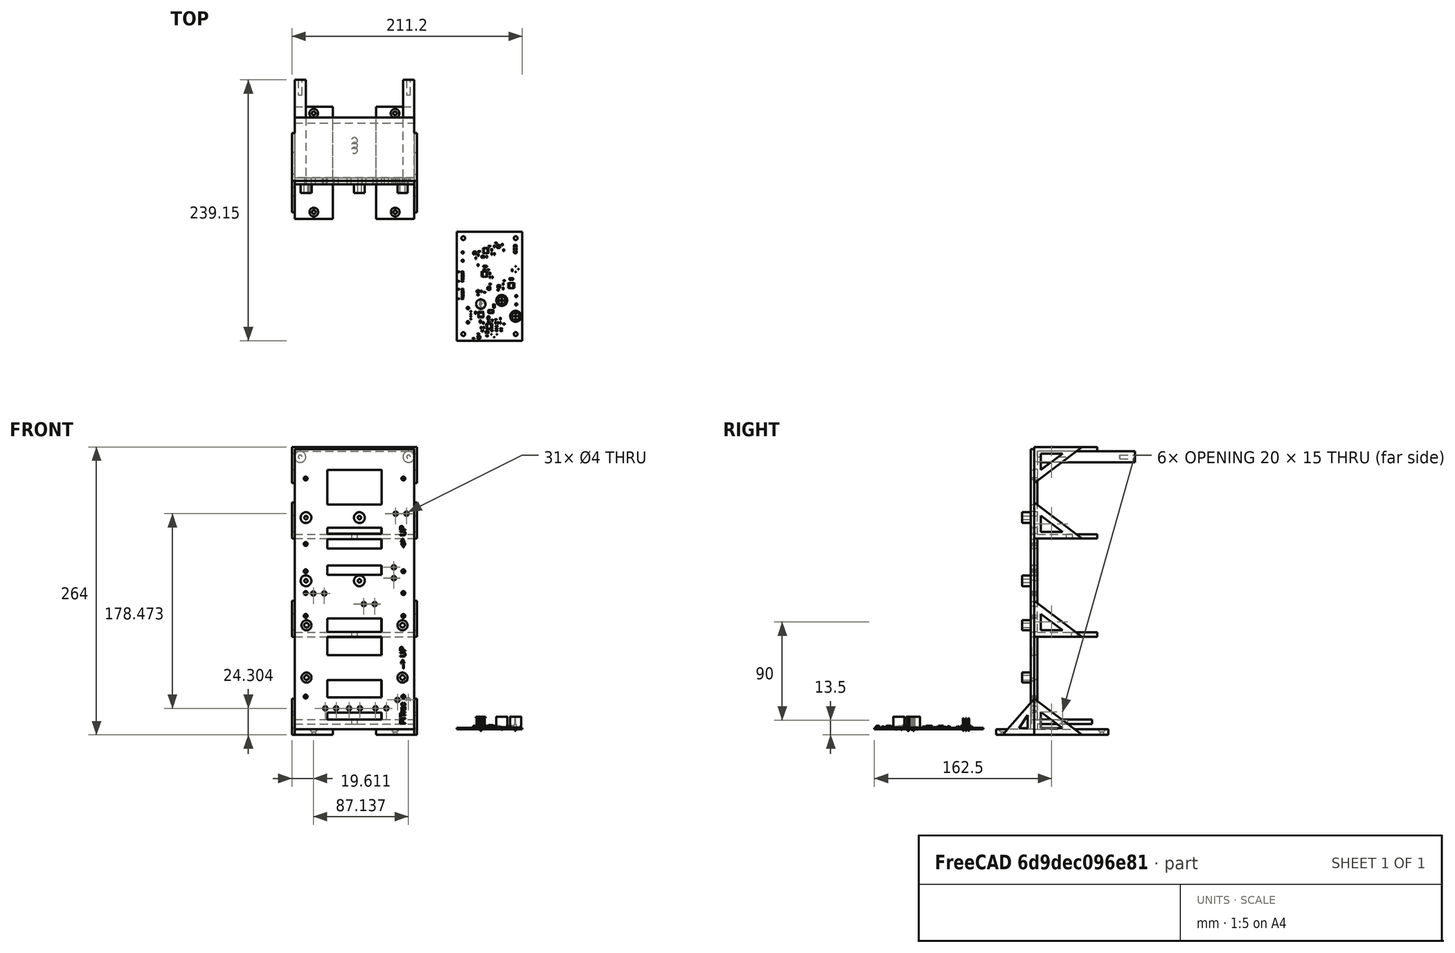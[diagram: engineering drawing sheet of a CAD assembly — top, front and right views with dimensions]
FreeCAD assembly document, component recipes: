
FREECAD ASSEMBLY — COMPONENT RECIPES ("Tower")

This assembly document has 2 components, labeled P0..P1 below (a component is one placed body or linked part). 1 of them carries a construction recipe — the FreeCAD feature program that regenerates the part from scratch, quoted from this document or its linked companion documents; the rest are supplied as boundary geometry only. No exploded tour is included for this assembly.
COMPONENT P0 — recipe-attached ("Tower Part -V2  Connector Board Variant", modeled in this document).
Construction recipe (the document's own serialized feature program — sketch geometry with constraints, then the solid features built on it; lengths are millimeters unless a unit is written):

FEATURE [Sketcher::SketchObject] Sketch  label="Backplate Sketch"
  ArcFitTolerance = 1e-06
  AttachmentSupport = -> [XZ_Plane001]
  FullyConstrained = false
  MakeInternals = false
  MapMode = 5
  Placement = pos=(0,0,0) rot=(1,0,0;1.5708rad)
  expr: Constraints[10] = <<Monitor Chassis Parameters>>.GSBackPlateBoltDiameter
  expr: Constraints[11] = <<Monitor Chassis Parameters>>.GSComputeBoardWidth / 2 - <<Monitor Chassis Parameters>>.GSBackPlateOuterHolesInsetFromSide
  expr: Constraints[129] = <<Monitor Chassis Parameters>>.GSTowerTieDownHoleSeparation
  expr: Constraints[15] = <<Monitor Chassis Parameters>>.GSBackPlateWidthIncrement
  expr: Constraints[55] = <<Monitor Chassis Parameters>>.GSBackPlateLengthIncrement
  expr: Constraints[59] = <<Monitor Chassis Parameters>>.GSBackPlateWidth
  expr: Constraints[71] = 1.5 * <<Monitor Chassis Parameters>>.GSBackPlateMinimumSpanWidth
  expr: Constraints[72] = 1.5 * <<Monitor Chassis Parameters>>.GSBackPlateMinimumSpanWidth
  expr: Constraints[7] = <<Monitor Chassis Parameters>>.GSComputeBoardHeight
  expr: Constraints[80] = <<Monitor Chassis Parameters>>.GSBackPlateLengthIncrement
  expr: Constraints[8] = <<Monitor Chassis Parameters>>.GSComputeBoardWidth
  expr: Constraints[97] = <<Monitor Chassis Parameters>>.GSTowerTieDownHoleDiameter
  expr: Constraints[98] = <<Monitor Chassis Parameters>>.GSTowerTieDownHoleDiameter
  expr: Constraints[99] = <<Monitor Chassis Parameters>>.GSTowerTieDownHoleSeparation
  expr: Constraints[9] = <<Monitor Chassis Parameters>>.GSComputeBoardWidth / 2
  sketch-geometry (63):
    g0: LineSegment [constr] StartX=-50.8 StartY=24.4067 StartZ=0 EndX=50.8 EndY=24.4067 EndZ=0
    g1: LineSegment [constr] StartX=50.8 StartY=24.4067 StartZ=0 EndX=50.8 EndY=253.007 EndZ=0
    g2: LineSegment [constr] StartX=50.8 StartY=253.007 StartZ=0 EndX=-50.8 EndY=253.007 EndZ=0
    g3: LineSegment [constr] StartX=-50.8 StartY=253.007 StartZ=0 EndX=-50.8 EndY=24.4067 EndZ=0
    g4: Circle CenterX=46.99 CenterY=45.5 CenterZ=0 NormalX=0 NormalY=0 NormalZ=1 AngleXU=0 Radius=1.4
    g5: LineSegment StartX=-54.8 StartY=257.007 StartZ=0 EndX=-54.8 EndY=20.4067 EndZ=0
    g6: LineSegment [constr] StartX=-54.8 StartY=20.4067 StartZ=0 EndX=54.8 EndY=20.4067 EndZ=0
    g7: LineSegment StartX=24.8 StartY=141.727 StartZ=0 EndX=-24.8 EndY=141.727 EndZ=0
    g8: LineSegment StartX=-24.8 StartY=141.727 StartZ=0 EndX=-24.8 EndY=150.228 EndZ=0
    g9: LineSegment StartX=-24.8 StartY=150.228 StartZ=0 EndX=24.8 EndY=150.228 EndZ=0
    g10: LineSegment StartX=24.8 StartY=150.228 StartZ=0 EndX=24.8 EndY=141.727 EndZ=0
    g11: LineSegment StartX=24.8 StartY=238.088 StartZ=0 EndX=-24.8 EndY=238.088 EndZ=0
    g12: LineSegment StartX=-24.8 StartY=238.088 StartZ=0 EndX=-24.8 EndY=206.336 EndZ=0
    g13: LineSegment StartX=-24.8 StartY=206.336 StartZ=0 EndX=24.8 EndY=206.336 EndZ=0
    g14: LineSegment StartX=24.8 StartY=206.336 StartZ=0 EndX=24.8 EndY=238.088 EndZ=0
    g15: LineSegment StartX=-24.8 StartY=184.895 StartZ=0 EndX=-24.8 EndY=179.263 EndZ=0
    g16: LineSegment StartX=-24.8 StartY=179.263 StartZ=0 EndX=24.8 EndY=179.263 EndZ=0
    g17: LineSegment StartX=24.8 StartY=179.263 StartZ=0 EndX=24.8 EndY=184.895 EndZ=0
    g18: LineSegment StartX=24.8 StartY=184.895 StartZ=0 EndX=-24.8 EndY=184.895 EndZ=0
    g19: LineSegment StartX=-24.8 StartY=84.8648 StartZ=0 EndX=-24.8 EndY=68.0887 EndZ=0
    g20: LineSegment StartX=-24.8 StartY=68.0887 StartZ=0 EndX=24.8 EndY=68.0887 EndZ=0
    g21: LineSegment StartX=24.8 StartY=68.0887 StartZ=0 EndX=24.8 EndY=84.8648 EndZ=0
    g22: LineSegment StartX=24.8 StartY=84.8648 StartZ=0 EndX=-24.8 EndY=84.8648 EndZ=0
    g23: LineSegment StartX=-24.8 StartY=45.1663 StartZ=0 EndX=-24.8 EndY=29.2968 EndZ=0
    g24: LineSegment StartX=24.8 StartY=29.2968 StartZ=0 EndX=24.8 EndY=45.1663 EndZ=0
    g25: LineSegment StartX=54.8 StartY=20.4067 StartZ=0 EndX=54.8 EndY=257.007 EndZ=0
    g26: LineSegment StartX=-54.8 StartY=257.007 StartZ=0 EndX=54.8 EndY=257.007 EndZ=0
    g27: LineSegment StartX=-54.8 StartY=20.4067 StartZ=0 EndX=-54.8 EndY=0 EndZ=0
    g28: LineSegment StartX=-54.8 StartY=0 StartZ=0 EndX=54.8 EndY=0 EndZ=0
    g29: LineSegment StartX=54.8 StartY=0 StartZ=0 EndX=54.8 EndY=20.4067 EndZ=0
    g30: LineSegment [constr] StartX=54.8 StartY=20.4067 StartZ=0 EndX=-54.8 EndY=20.4067 EndZ=0
    g31: LineSegment StartX=-24.8 StartY=45.1663 StartZ=0 EndX=24.8 EndY=45.1663 EndZ=0
    g32: LineSegment StartX=-24.8 StartY=29.2968 StartZ=0 EndX=24.8 EndY=29.2968 EndZ=0
    g33: LineSegment StartX=-24.8 StartY=15.5143 StartZ=0 EndX=-24.8 EndY=9.05652 EndZ=0
    g34: LineSegment StartX=-24.8 StartY=9.05652 StartZ=0 EndX=24.8 EndY=9.05652 EndZ=0
    g35: LineSegment StartX=24.8 StartY=9.05652 StartZ=0 EndX=24.8 EndY=15.5143 EndZ=0
    g36: LineSegment StartX=24.8 StartY=15.5143 StartZ=0 EndX=-24.8 EndY=15.5143 EndZ=0
    g37: Circle CenterX=37.7226 CenterY=197.777 CenterZ=0 NormalX=0 NormalY=0 NormalZ=1 AngleXU=0 Radius=2
    g38: Circle CenterX=47.7226 CenterY=197.777 CenterZ=0 NormalX=0 NormalY=0 NormalZ=1 AngleXU=0 Radius=2
    g39: Circle CenterX=-4.99066 CenterY=19.304 CenterZ=0 NormalX=0 NormalY=0 NormalZ=1 AngleXU=0 Radius=2
    g40: Circle CenterX=5.00934 CenterY=19.304 CenterZ=0 NormalX=0 NormalY=0 NormalZ=1 AngleXU=0 Radius=2
    g41: Circle CenterX=19.2048 CenterY=19.304 CenterZ=0 NormalX=0 NormalY=0 NormalZ=1 AngleXU=0 Radius=2
    g42: Circle CenterX=29.2048 CenterY=19.304 CenterZ=0 NormalX=0 NormalY=0 NormalZ=1 AngleXU=0 Radius=2
    g43: Circle CenterX=39.3678 CenterY=26.9682 CenterZ=0 NormalX=0 NormalY=0 NormalZ=1 AngleXU=0 Radius=2
    g44: Circle CenterX=49.3678 CenterY=26.9682 CenterZ=0 NormalX=0 NormalY=0 NormalZ=1 AngleXU=0 Radius=2
    g45: Circle CenterX=-37.7708 CenterY=124.614 CenterZ=0 NormalX=0 NormalY=0 NormalZ=1 AngleXU=0 Radius=2
    g46: Circle CenterX=-27.7708 CenterY=124.614 CenterZ=0 NormalX=0 NormalY=0 NormalZ=1 AngleXU=0 Radius=2
    g47: Circle CenterX=-26.8243 CenterY=19.304 CenterZ=0 NormalX=0 NormalY=0 NormalZ=1 AngleXU=0 Radius=2
    g48: Circle CenterX=-16.8243 CenterY=19.304 CenterZ=0 NormalX=0 NormalY=0 NormalZ=1 AngleXU=0 Radius=2
    g49: Circle CenterX=36.1106 CenterY=138.665 CenterZ=0 NormalX=0 NormalY=0 NormalZ=1 AngleXU=0 Radius=2
    g50: Circle CenterX=36.1106 CenterY=148.665 CenterZ=0 NormalX=0 NormalY=0 NormalZ=1 AngleXU=0 Radius=2
    g51: Circle CenterX=49.3678 CenterY=26.9682 CenterZ=0 NormalX=0 NormalY=0 NormalZ=1 AngleXU=0 Radius=2
    g52: Circle CenterX=8.52821 CenterY=114.871 CenterZ=0 NormalX=0 NormalY=0 NormalZ=1 AngleXU=0 Radius=2
    g53: Circle CenterX=18.5282 CenterY=114.871 CenterZ=0 NormalX=0 NormalY=0 NormalZ=1 AngleXU=0 Radius=2
    g54: Circle CenterX=49.3678 CenterY=26.9682 CenterZ=0 NormalX=0 NormalY=0 NormalZ=1 AngleXU=0 Radius=2
    g55: LineSegment StartX=-24.8 StartY=174.457 StartZ=0 EndX=-24.8 EndY=165.919 EndZ=0
    g56: LineSegment StartX=-24.8 StartY=165.919 StartZ=0 EndX=24.8 EndY=165.919 EndZ=0
    g57: LineSegment StartX=24.8 StartY=165.919 StartZ=0 EndX=24.8 EndY=174.457 EndZ=0
    g58: LineSegment StartX=24.8 StartY=174.457 StartZ=0 EndX=-24.8 EndY=174.457 EndZ=0
    g59: LineSegment StartX=-24.8 StartY=101.627 StartZ=0 EndX=-24.8 EndY=89.2697 EndZ=0
    g60: LineSegment StartX=-24.8 StartY=89.2697 StartZ=0 EndX=24.8 EndY=89.2697 EndZ=0
    g61: LineSegment StartX=24.8 StartY=89.2697 StartZ=0 EndX=24.8 EndY=101.627 EndZ=0
    g62: LineSegment StartX=24.8 StartY=101.627 StartZ=0 EndX=-24.8 EndY=101.627 EndZ=0
  constraints (152):
    c: Coincident(g0,g1)
    c: Coincident(g1,g2)
    c: Coincident(g2,g3)
    c: Coincident(g3,g0)
    c: Horizontal(g2)
    c: Vertical(g1)
    c: Vertical(g3)
    c: DistanceY(g0,g2) = 228.6
    c: DistanceX(g0,g0) = 101.6
    c: DistanceX(g0,g-1) = 50.8
    c: Diameter(g4) = 2.8
    c: DistanceX(g-1,g4) = 46.99
    c: Coincident(g5,g6)
    c: Vertical(g5)
    c: Horizontal(g6)
    c: DistanceX(g5,g0) = 4
    c: Horizontal(g0)
    c: Coincident(g7,g8)
    c: Coincident(g8,g9)
    c: Coincident(g9,g10)
    c: Coincident(g10,g7)
    c: Horizontal(g7)
    c: Vertical(g8)
    c: Vertical(g10)
    c: Coincident(g11,g12)
    c: Coincident(g12,g13)
    c: Coincident(g13,g14)
    c: Coincident(g14,g11)
    c: Horizontal(g11)
    c: Horizontal(g13)
    c: Vertical(g12)
    c: Vertical(g14)
    c: Coincident(g15,g16)
    c: Coincident(g16,g17)
    c: Coincident(g17,g18)
    c: Coincident(g18,g15)
    c: Vertical(g15)
    c: Vertical(g17)
    c: Horizontal(g16)
    c: Coincident(g19,g20)
    c: Coincident(g20,g21)
    c: Coincident(g21,g22)
    c: Coincident(g22,g19)
    c: Vertical(g19)
    c: Vertical(g21)
    c: Horizontal(g20)
    c: Horizontal(g22)
    c: Vertical(g23)
    c: Vertical(g24)
    c: Vertical(g15,g19)
    c: Vertical(g19,g23)
    c: Vertical(g7,g21)
    c: Vertical(g21,g24)
    c: Coincident(g25,g6)
    c: Vertical(g25)
    c: DistanceY(g1,g25) = 4
    c: Horizontal(g5,g25)
    c: Coincident(g26,g5)
    c: Coincident(g26,g25)
    c: DistanceX(g5,g6) = 109.6
    c: Coincident(g27,g28)
    c: Coincident(g28,g29)
    c: Coincident(g29,g30)
    c: Coincident(g30,g27)
    c: Vertical(g27)
    c: Vertical(g29)
    c: Horizontal(g28)
    c: Horizontal(g30)
    c: Coincident(g27,g5)
    c: Horizontal(g28,g-1)
    c: Vertical(g29,g6)
    c: DistanceX(g5,g11) = 30
    c: DistanceX(g11,g25) = 30
    c: Horizontal(g9)
    c: Coincident(g31,g23)
    c: Coincident(g31,g24)
    c: Horizontal(g31)
    c: Vertical(g11,g15)
    c: Vertical(g11,g9)
    c: Vertical(g16,g9)
    c: DistanceY(g5,g0) = 4
    c: Coincident(g32,g23)
    c: Coincident(g32,g24)
    c: Horizontal(g32)
    c: Horizontal(g18)
    c: Vertical(g15,g8)
    c: Coincident(g33,g34)
    c: Coincident(g34,g35)
    c: Coincident(g35,g36)
    c: Coincident(g36,g33)
    c: Vertical(g33)
    c: Vertical(g35)
    c: Horizontal(g34)
    c: Horizontal(g36)
    c: Vertical(g23,g33)
    c: Vertical(g24,g35)
    c: Horizontal(g37,g38)
    c: Diameter(g37) = 4
    c: Diameter(g38) = 4
    c: DistanceX(g37,g38) = 10
    c: Horizontal(g39,g40)
    c: Diameter(g39) = 4
    c: Diameter(g40) = 4
    c: DistanceX(g39,g40) = 10
    c: Horizontal(g41,g42)
    c: Diameter(g41) = 4
    c: Diameter(g42) = 4
    c: DistanceX(g41,g42) = 10
    c: Horizontal(g43,g44)
    c: Diameter(g43) = 4
    c: Diameter(g44) = 4
    c: DistanceX(g43,g44) = 10
    c: Horizontal(g45,g46)
    c: Diameter(g45) = 4
    c: Diameter(g46) = 4
    c: DistanceX(g45,g46) = 10
    c: Horizontal(g47,g48)
    c: Diameter(g47) = 4
    c: Diameter(g48) = 4
    c: DistanceX(g47,g48) = 10
    c: Diameter(g49) = 4
    c: Diameter(g50) = 4
    c: Diameter(g51) = 4
    c: Horizontal(g52,g53)
    c: Diameter(g52) = 4
    c: Diameter(g53) = 4
    c: DistanceX(g52,g53) = 10
    c: Diameter(g54) = 4
    c: Vertical(g50,g49)
    c: DistanceY(g49,g50) = 10
    c: Horizontal(g48,g39)
    c: Horizontal(g40,g41)
    c: Coincident(g55,g56)
    c: Coincident(g56,g57)
    c: Coincident(g57,g58)
    c: Coincident(g58,g55)
    c: Vertical(g55)
    c: Vertical(g57)
    c: Horizontal(g56)
    c: Horizontal(g58)
    c: Vertical(g8,g55)
    c: Vertical(g9,g56)
    c: Coincident(g59,g60)
    c: Coincident(g60,g61)
    c: Coincident(g61,g62)
    c: Coincident(g62,g59)
    c: Vertical(g59)
    c: Vertical(g61)
    c: Horizontal(g60)
    c: Horizontal(g62)
    c: Vertical(g20,g60)
    c: Vertical(g19,g59)
FEATURE [PartDesign::Pad] Pad  label="Backplate Pad"
  Direction = (0,-1,2e-16)
  Length = 3
  Length2 = 10
  Placement = pos=(0,0,0) rot=(1,0,0;1.5708rad)
  Profile = -> Sketch
  ReferenceAxis = -> Sketch [N_Axis]
  Reversed = true
  Suppressed = false
  Type = 0
  expr: Length = <<Monitor Chassis Parameters>>.GSBackPlateThickness
FEATURE [Sketcher::SketchObject] Sketch001  label="Backplate Risers Sketch"
  ArcFitTolerance = 1e-06
  AttachmentSupport = -> [XZ_Plane001]
  FullyConstrained = false
  MakeInternals = false
  MapMode = 5
  Placement = pos=(0,0,0) rot=(1,0,0;1.5708rad)
  expr: Constraints[12] = <<Monitor Chassis Parameters>>.GSPi5MountingRiserOutsideDiameter
  expr: Constraints[13] = <<Monitor Chassis Parameters>>.GSPi5MountingRiserOutsideDiameter
  expr: Constraints[14] = <<Monitor Chassis Parameters>>.GSPi5MountingRiserOutsideDiameter
  expr: Constraints[18] = <<Monitor Chassis Parameters>>.GSPi5MountingHoleCenterLength
  expr: Constraints[19] = <<Monitor Chassis Parameters>>.GSPi5MountingRiserOutsideDiameter
  expr: Constraints[21] = <<Monitor Chassis Parameters>>.GsPi5MountingHoleDiameter
  expr: Constraints[25] = <<Monitor Chassis Parameters>>.GSConnectorBoardMountingRiserOutsideDiameter
  expr: Constraints[26] = <<Monitor Chassis Parameters>>.GSConnectorBoardMountingHoleDiameter
  expr: Constraints[28] = <<Monitor Chassis Parameters>>.GSConnectorBoardMountingRiserOutsideDiameter
  expr: Constraints[29] = <<Monitor Chassis Parameters>>.GSConnectorBoardMountingHoleDiameter
  expr: Constraints[31] = <<Monitor Chassis Parameters>>.GSConnectorBoardMountingRiserOutsideDiameter
  expr: Constraints[32] = <<Monitor Chassis Parameters>>.GSConnectorBoardMountingHoleDiameter
  expr: Constraints[34] = <<Monitor Chassis Parameters>>.GSConnectorBoardMountingRiserOutsideDiameter
  expr: Constraints[35] = <<Monitor Chassis Parameters>>.GSConnectorBoardMountingHoleDiameter
  expr: Constraints[38] = <<Monitor Chassis Parameters>>.GsV2ConnectorBoardMountingHoleSeparationX
  expr: Constraints[39] = <<Monitor Chassis Parameters>>.GsV2ConnectorBoardMountingHoleSeparationY
  expr: Constraints[40] = 0.5 * <<Monitor Chassis Parameters>>.GSComputeBoardWidth - 0.5 * (<<Monitor Chassis Parameters>>.GSComputeBoardWidth - <<Monitor Chassis Parameters>>.GsV2ConnectorBoardMountingHoleSeparationX)
  expr: Constraints[41] = <<Monitor Chassis Parameters>>.GSPi5MountingHoleCenterWidth
  expr: Constraints[44] = 20 + 0.5 * <<Monitor Chassis Parameters>>.GSComputeBoardWidth - 0.5 * (<<Monitor Chassis Parameters>>.GSComputeBoardWidth - <<Monitor Chassis Parameters>>.GSPi5MountingHoleCenterWidth)
  expr: Constraints[5] = <<Monitor Chassis Parameters>>.GsPi5MountingHoleDiameter
  expr: Constraints[6] = <<Monitor Chassis Parameters>>.GsPi5MountingHoleDiameter
  expr: Constraints[7] = <<Monitor Chassis Parameters>>.GsPi5MountingHoleDiameter
  sketch-geometry (20):
    g0: LineSegment [constr] StartX=-50.8 StartY=20 StartZ=0 EndX=50.8 EndY=20 EndZ=0
    g1: LineSegment [constr] StartX=50.8 StartY=20 StartZ=0 EndX=50.8 EndY=248.6 EndZ=0
    g2: LineSegment [constr] StartX=50.8 StartY=248.6 StartZ=0 EndX=-50.8 EndY=248.6 EndZ=0
    g3: LineSegment [constr] StartX=-50.8 StartY=248.6 StartZ=0 EndX=-50.8 EndY=20 EndZ=0
    g4: Circle CenterX=-44.5 CenterY=136.223 CenterZ=0 NormalX=0 NormalY=0 NormalZ=1 AngleXU=0 Radius=1.575
    g5: Circle CenterX=4.5 CenterY=136.223 CenterZ=0 NormalX=0 NormalY=0 NormalZ=1 AngleXU=0 Radius=1.575
    g6: Circle CenterX=-44.5 CenterY=194.223 CenterZ=0 NormalX=0 NormalY=0 NormalZ=1 AngleXU=0 Radius=1.575
    g7: Circle CenterX=-44.5 CenterY=194.223 CenterZ=0 NormalX=0 NormalY=0 NormalZ=1 AngleXU=0 Radius=4.95
    g8: Circle CenterX=-44.5 CenterY=136.223 CenterZ=0 NormalX=0 NormalY=0 NormalZ=1 AngleXU=0 Radius=4.95
    g9: Circle CenterX=4.5 CenterY=136.223 CenterZ=0 NormalX=0 NormalY=0 NormalZ=1 AngleXU=0 Radius=4.95
    g10: Circle CenterX=4.5 CenterY=194.223 CenterZ=0 NormalX=0 NormalY=0 NormalZ=1 AngleXU=0 Radius=4.95
    g11: Circle CenterX=4.5 CenterY=194.223 CenterZ=0 NormalX=0 NormalY=0 NormalZ=1 AngleXU=0 Radius=1.575
    g12: Circle CenterX=-44 CenterY=47.4737 CenterZ=0 NormalX=0 NormalY=0 NormalZ=1 AngleXU=0 Radius=2.125
    g13: Circle CenterX=-44 CenterY=47.4737 CenterZ=0 NormalX=0 NormalY=0 NormalZ=1 AngleXU=0 Radius=4.625
    g14: Circle CenterX=44 CenterY=47.4737 CenterZ=0 NormalX=0 NormalY=0 NormalZ=1 AngleXU=0 Radius=2.125
    g15: Circle CenterX=44 CenterY=47.4737 CenterZ=0 NormalX=0 NormalY=0 NormalZ=1 AngleXU=0 Radius=4.625
    g16: Circle CenterX=44 CenterY=95.4737 CenterZ=0 NormalX=0 NormalY=0 NormalZ=1 AngleXU=0 Radius=2.125
    g17: Circle CenterX=44 CenterY=95.4737 CenterZ=0 NormalX=0 NormalY=0 NormalZ=1 AngleXU=0 Radius=4.625
    g18: Circle CenterX=-44 CenterY=95.4737 CenterZ=0 NormalX=0 NormalY=0 NormalZ=1 AngleXU=0 Radius=2.125
    g19: Circle CenterX=-44 CenterY=95.4737 CenterZ=0 NormalX=0 NormalY=0 NormalZ=1 AngleXU=0 Radius=4.625
  constraints (45):
    c: Coincident(g0,g1)
    c: Coincident(g1,g2)
    c: Coincident(g3,g0)
    c: Vertical(g1)
    c: Vertical(g3)
    c: Diameter(g4) = 3.15
    c: Diameter(g5) = 3.15
    c: Diameter(g6) = 3.15
    c: Horizontal(g0)
    c: Coincident(g7,g6)
    c: Coincident(g8,g4)
    c: Coincident(g9,g5)
    c: Diameter(g9) = 9.9
    c: Diameter(g8) = 9.9
    c: Diameter(g7) = 9.9
    c: Horizontal(g5,g4)
    c: Horizontal(g2,g1)
    c: Vertical(g6,g4)
    c: DistanceY(g4,g6) = 58
    c: Diameter(g10) = 9.9
    c: Coincident(g11,g10)
    c: Diameter(g11) = 3.15
    c: Horizontal(g10,g6)
    c: Vertical(g10,g5)
    c: Coincident(g13,g12)
    c: Diameter(g13) = 9.25
    c: Diameter(g12) = 4.25
    c: Coincident(g15,g14)
    c: Diameter(g15) = 9.25
    c: Diameter(g14) = 4.25
    c: Coincident(g17,g16)
    c: Diameter(g17) = 9.25
    c: Diameter(g16) = 4.25
    c: Coincident(g19,g18)
    c: Diameter(g19) = 9.25
    c: Diameter(g18) = 4.25
    c: Horizontal(g16,g18)
    c: Horizontal(g14,g12)
    c: DistanceX(g18,g16) = 88
    c: DistanceY(g12,g18) = 48
    c: DistanceX(g18,g-1) = 44
    c: DistanceX(g6,g10) = 49
    c: Vertical(g12,g18)
    c: Vertical(g16,g14)
    c: DistanceX(g4,g-1) = 44.5
FEATURE [PartDesign::Pad] Pad001  label="Backplate Risers Pad"
  BaseFeature = -> Pad
  Direction = (0,-1,2e-16)
  Length = 8
  Length2 = 10
  Placement = pos=(0,0,0) rot=(1,0,0;1.5708rad)
  Profile = -> Sketch001
  ReferenceAxis = -> Sketch001 [N_Axis]
  Suppressed = false
  Type = 0
  expr: Length = <<Monitor Chassis Parameters>>.GSBackPlateConnectorBoardVariantStandoffHeight
FEATURE [Sketcher::SketchObject] Sketch002  label="Backplate Foot Sketch"
  ArcFitTolerance = 1e-06
  AttachmentSupport = -> [XZ_Plane001]
  FullyConstrained = true
  MakeInternals = false
  MapMode = 5
  Placement = pos=(0,0,0) rot=(1,0,0;1.5708rad)
  expr: Constraints[11] = <<Monitor Chassis Parameters>>.GSTowerFeetThickness
  expr: Constraints[21] = <<Monitor Chassis Parameters>>.GSTowerFeetThickness
  expr: Constraints[22] = <<Monitor Chassis Parameters>>.GSBackPlateFootWidth
  expr: Constraints[23] = 0.5 * <<Monitor Chassis Parameters>>.GSBackPlateWidth
  expr: Constraints[8] = <<Monitor Chassis Parameters>>.GSBackPlateFootWidth
  expr: Constraints[9] = 0.5 * <<Monitor Chassis Parameters>>.GSBackPlateWidth
  sketch-geometry (8):
    g0: LineSegment StartX=-54.8 StartY=-5 StartZ=0 EndX=-19.8 EndY=-5 EndZ=0
    g1: LineSegment StartX=-19.8 StartY=-5 StartZ=0 EndX=-19.8 EndY=0 EndZ=0
    g2: LineSegment StartX=-19.8 StartY=0 StartZ=0 EndX=-54.8 EndY=0 EndZ=0
    g3: LineSegment StartX=-54.8 StartY=0 StartZ=0 EndX=-54.8 EndY=-5 EndZ=0
    g4: LineSegment StartX=54.8 StartY=-5 StartZ=0 EndX=54.8 EndY=0 EndZ=0
    g5: LineSegment StartX=54.8 StartY=0 StartZ=0 EndX=19.8 EndY=0 EndZ=0
    g6: LineSegment StartX=19.8 StartY=0 StartZ=0 EndX=19.8 EndY=-5 EndZ=0
    g7: LineSegment StartX=19.8 StartY=-5 StartZ=0 EndX=54.8 EndY=-5 EndZ=0
  constraints (24):
    c: Coincident(g0,g1)
    c: Coincident(g1,g2)
    c: Coincident(g2,g3)
    c: Coincident(g3,g0)
    c: Horizontal(g0)
    c: Horizontal(g2)
    c: Vertical(g1)
    c: Vertical(g3)
    c: DistanceX(g2,g1) = 35
    c: DistanceX(g2,g-1) = 54.8
    c: Horizontal(g2,g-1)
    c: DistanceY(g0,g2) = 5
    c: Coincident(g4,g5)
    c: Coincident(g5,g6)
    c: Coincident(g6,g7)
    c: Coincident(g7,g4)
    c: Vertical(g4)
    c: Vertical(g6)
    c: Horizontal(g5)
    c: Horizontal(g7)
    c: Horizontal(g5,g-1)
    c: DistanceY(g4,g4) = 5
    c: DistanceX(g6,g4) = 35
    c: DistanceX(g-1,g4) = 54.8
FEATURE [PartDesign::Pad] Pad002  label="Backplate Foot Pad"
  BaseFeature = -> Pad001
  Direction = (0,-1,2e-16)
  Length = 32
  Length2 = 3
  Placement = pos=(0,0,0) rot=(1,0,0;1.5708rad)
  Profile = -> Sketch002
  ReferenceAxis = -> Sketch002 [N_Axis]
  Suppressed = false
  Type = 4
  expr: Length = <<Monitor Chassis Parameters>>.GSBackPlateFootLengthBackward
  expr: Length2 = <<Monitor Chassis Parameters>>.GSBackPlateThickness
FEATURE [Sketcher::SketchObject] Sketch003  label="Backplate Foot Screw Holes Sketch"
  ArcFitTolerance = 1e-06
  AttachmentSupport = -> [XY_Plane001]
  FullyConstrained = true
  MakeInternals = false
  MapMode = 5
  expr: Constraints[0] = 0.8 * <<Monitor Chassis Parameters>>.GSBackPlateFootLengthBackward
  expr: Constraints[1] = 0.5 * <<Monitor Chassis Parameters>>.GSBackPlateWidth - 0.5 * <<Monitor Chassis Parameters>>.GSBackPlateFootWidth
  expr: Constraints[2] = 0.5 * <<Monitor Chassis Parameters>>.GSBackPlateWidth - 0.5 * <<Monitor Chassis Parameters>>.GSBackPlateFootWidth
  expr: Constraints[3] = <<Monitor Chassis Parameters>>.GSTowerFeetScrewDiameter
  expr: Constraints[4] = <<Monitor Chassis Parameters>>.GSTowerFeetScrewDiameter
  sketch-geometry (2):
    g0: Circle CenterX=-37.3 CenterY=-25.6 CenterZ=0 NormalX=0 NormalY=0 NormalZ=1 AngleXU=0 Radius=1.7
    g1: Circle CenterX=37.3 CenterY=-25.6 CenterZ=0 NormalX=0 NormalY=0 NormalZ=1 AngleXU=0 Radius=1.7
  constraints (6):
    c: DistanceY(g0,g-1) = 25.6
    c: DistanceX(g0,g-1) = 37.3
    c: DistanceX(g-1,g1) = 37.3
    c: Diameter(g0) = 3.4
    c: Diameter(g1) = 3.4
    c: Horizontal(g1,g0)
FEATURE [PartDesign::Hole] Hole  label="Backplate Foot Screw Holes"
  BaseFeature = -> Pad002
  CustomThreadClearance = 0
  Depth = 25
  DepthType = 0
  Diameter = 3.4
  DrillForDepth = false
  DrillPoint = 1
  DrillPointAngle = 118
  HoleCutCountersinkAngle = 90
  HoleCutCustomValues = false
  HoleCutDepth = 0
  HoleCutDiameter = 8
  HoleCutType = 2
  ModelThread = false
  Placement = pos=(0,0,0) rot=(1,0,0;1.5708rad)
  Profile = -> Sketch003
  Suppressed = false
  Tapered = false
  TaperedAngle = 90
  ThreadClass = 0
  ThreadDepth = 25
  ThreadDepthType = 0
  ThreadDirection = 0
  ThreadFit = 0
  ThreadSize = 0
  ThreadType = 0
  Threaded = false
  UseCustomThreadClearance = false
  expr: Diameter = <<Monitor Chassis Parameters>>.GSTowerFeetScrewDiameter
  expr: HoleCutDiameter = <<Monitor Chassis Parameters>>.GSM4BoltCountersinkDiameter
FEATURE [PartDesign::Plane] DatumPlane
  AttachmentOffset = pos=(0,0,54.8) rot=(0,0,1;0rad)
  AttachmentSupport = -> [YZ_Plane001]
  Length = 73.939
  MapMode = 5
  Placement = pos=(54.8,0,0) rot=(0.57735,0.57735,0.57735;2.0944rad)
  ResizeMode = 0
  Width = 245.788
  expr: .AttachmentOffset.Base.z = 0.5 * <<Monitor Chassis Parameters>>.GSBackPlateWidth
FEATURE [Sketcher::SketchObject] Sketch004  label="Foot Support Corner Sketch"
  ArcFitTolerance = 1e-06
  AttachmentSupport = -> [DatumPlane]
  FullyConstrained = true
  MakeInternals = false
  MapMode = 5
  Placement = pos=(54.8,0,0) rot=(0.57735,0.57735,0.57735;2.0944rad)
  expr: Constraints[14] = <<Monitor Chassis Parameters>>.GSSideCornerCutoutInset
  expr: Constraints[15] = <<Monitor Chassis Parameters>>.GSSideCornerCutoutInset
  expr: Constraints[16] = 2.5 * <<Monitor Chassis Parameters>>.GSSideCornerCutoutInset
  expr: Constraints[17] = 2.5 * <<Monitor Chassis Parameters>>.GSSideCornerCutoutInset
  expr: Constraints[1] = <<Monitor Chassis Parameters>>.GSBackPlateThickness
  expr: Constraints[4] = <<Monitor Chassis Parameters>>.GSTowerFeetThickness
  expr: Constraints[7] = 0.9 * <<Monitor Chassis Parameters>>.GSBackPlateFootLengthBackward
  expr: Constraints[8] = 0.6 * <<Monitor Chassis Parameters>>.GSTowerFloorDepth
  sketch-geometry (6):
    g0: LineSegment StartX=-25.8 StartY=-5 StartZ=0 EndX=3 EndY=-5 EndZ=0
    g1: LineSegment StartX=3 StartY=28 StartZ=0 EndX=3 EndY=-5 EndZ=0
    g2: LineSegment StartX=-25.8 StartY=-5 StartZ=0 EndX=3 EndY=28 EndZ=0
    g3: LineSegment StartX=-10.8 StartY=1 StartZ=0 EndX=-3 EndY=13 EndZ=0
    g4: LineSegment StartX=-3 StartY=13 StartZ=0 EndX=-3 EndY=1 EndZ=0
    g5: LineSegment StartX=-10.8 StartY=1 StartZ=0 EndX=-3 EndY=1 EndZ=0
  constraints (18):
    c: Horizontal(g0)
    c: DistanceX(g-1,g0) = 3
    c: Coincident(g1,g0)
    c: Vertical(g1)
    c: DistanceY(g0,g-1) = 5
    c: Coincident(g2,g0)
    c: Coincident(g2,g1)
    c: DistanceX(g0,g0) = 28.8
    c: DistanceY(g0,g1) = 33
    c: Coincident(g4,g3)
    c: Vertical(g4)
    c: Coincident(g5,g3)
    c: Coincident(g5,g4)
    c: Horizontal(g5)
    c: DistanceY(g0,g4) = 6
    c: DistanceX(g4,g0) = 6
    c: DistanceX(g0,g3) = 15
    c: DistanceY(g3,g1) = 15
FEATURE [PartDesign::Pad] Pad003  label="Foot Support Corner Pad"
  BaseFeature = -> Hole
  Direction = (1,0,0)
  Length = 2.5
  Length2 = 10
  Placement = pos=(0,0,0) rot=(1,0,0;1.5708rad)
  Profile = -> Sketch004
  ReferenceAxis = -> Sketch004 [N_Axis]
  Suppressed = false
  Type = 0
  expr: Length = <<Monitor Chassis Parameters>>.GSSideCornerThickness
FEATURE [PartDesign::Mirrored] Mirrored  label="Foot Support Corner Mirrored"
  BaseFeature = -> Pad003
  MirrorPlane = -> YZ_Plane001
  Originals = -> [Pad003]
  Placement = pos=(0,0,0) rot=(1,0,0;1.5708rad)
  Suppressed = false
  TransformMode = 0
FEATURE [PartDesign::Plane] DatumPlane001
  AttachmentOffset = pos=(0,0,54.8) rot=(0,0,1;0rad)
  AttachmentSupport = -> [YZ_Plane002]
  Length = 82.8329
  MapMode = 5
  Placement = pos=(54.8,0,0) rot=(0.57735,0.57735,0.57735;2.0944rad)
  ResizeMode = 0
  Width = 201.085
  expr: .AttachmentOffset.Base.z = 0.5 * <<Monitor Chassis Parameters>>.GSBackPlateWidth
FEATURE [Sketcher::SketchObject] Sketch005  label="Frontplate Sketch"
  ArcFitTolerance = 1e-06
  AttachmentSupport = -> [XZ_Plane002]
  FullyConstrained = false
  MakeInternals = false
  MapMode = 5
  Placement = pos=(0,0,0) rot=(1,0,0;1.5708rad)
  expr: Constraints[103] = <<Monitor Chassis Parameters>>.GSTowerLayerJoinScrewDiameter
  expr: Constraints[104] = <<Monitor Chassis Parameters>>.GSTowerLayerJoinScrewDiameter
  expr: Constraints[106] = <<Monitor Chassis Parameters>>.GSTowerLayerJoinScrewHeightFromFoot_1
  expr: Constraints[107] = <<Monitor Chassis Parameters>>.GSTowerLayerJoinScrewHeightFromFoot_3
  expr: Constraints[109] = <<Monitor Chassis Parameters>>.GSTowerLayerJoinScrewHeightFromFoot_4
  expr: Constraints[110] = <<Monitor Chassis Parameters>>.GSTowerLayerJoinScrewHeightFromFoot_5
  expr: Constraints[112] = <<Monitor Chassis Parameters>>.GSTowerLayerJoinScrewDiameter
  expr: Constraints[113] = <<Monitor Chassis Parameters>>.GSTowerLayerJoinScrewDiameter
  expr: Constraints[116] = <<Monitor Chassis Parameters>>.GSTowerLayerJoinScrewHeightFromFoot_6
  expr: Constraints[128] = <<Monitor Chassis Parameters>>.GSTowerLayerJoinScrewDiameter
  expr: Constraints[133] = <<Monitor Chassis Parameters>>.GSTowerLayerJoinScrewHeightFromFoot_2
  expr: Constraints[134] = <<Monitor Chassis Parameters>>.GSTowerTieDownHoleDiameter
  expr: Constraints[135] = <<Monitor Chassis Parameters>>.GSTowerTieDownHoleDiameter
  expr: Constraints[13] = <<Monitor Chassis Parameters>>.GSBackPlateWidthIncrement
  expr: Constraints[141] = <<Monitor Chassis Parameters>>.GSTowerTieDownHoleSeparation
  expr: Constraints[60] = <<Monitor Chassis Parameters>>.GSBackPlateLengthIncrement
  expr: Constraints[64] = <<Monitor Chassis Parameters>>.GSBackPlateWidth
  expr: Constraints[65] = <<Monitor Chassis Parameters>>.GSBackPlateVerticalOffset
  expr: Constraints[7] = <<Monitor Chassis Parameters>>.GSComputeBoardHeight
  expr: Constraints[84] = 1.5 * <<Monitor Chassis Parameters>>.GSFrontPlateMinimumSpanWidth
  expr: Constraints[85] = 1.5 * <<Monitor Chassis Parameters>>.GSFrontPlateMinimumSpanWidth
  expr: Constraints[89] = <<Monitor Chassis Parameters>>.GSTowerFourthFloorHeight + <<Monitor Chassis Parameters>>.GSTowerFloorThickness
  expr: Constraints[8] = <<Monitor Chassis Parameters>>.GSComputeBoardWidth
  expr: Constraints[90] = <<Monitor Chassis Parameters>>.GSTowerLayerJoinScrewDiameter
  expr: Constraints[91] = <<Monitor Chassis Parameters>>.GSTowerLayerJoinScrewDiameter
  expr: Constraints[93] = <<Monitor Chassis Parameters>>.GSTowerLayerJoinScrewInset
  expr: Constraints[94] = <<Monitor Chassis Parameters>>.GSTowerLayerJoinScrewInset
  expr: Constraints[95] = <<Monitor Chassis Parameters>>.GSTowerLayerJoinScrewDiameter
  expr: Constraints[96] = <<Monitor Chassis Parameters>>.GSTowerLayerJoinScrewDiameter
  expr: Constraints[98] = <<Monitor Chassis Parameters>>.GSTowerLayerJoinScrewDiameter
  expr: Constraints[99] = <<Monitor Chassis Parameters>>.GSTowerLayerJoinScrewDiameter
  expr: Constraints[9] = <<Monitor Chassis Parameters>>.GSComputeBoardWidth / 2
  sketch-geometry (75):
    g0: LineSegment [constr] StartX=-50.8 StartY=24 StartZ=0 EndX=50.8 EndY=24 EndZ=0
    g1: LineSegment [constr] StartX=50.8 StartY=24 StartZ=0 EndX=50.8 EndY=252.6 EndZ=0
    g2: LineSegment [constr] StartX=50.8 StartY=252.6 StartZ=0 EndX=-50.8 EndY=252.6 EndZ=0
    g3: LineSegment [constr] StartX=-50.8 StartY=252.6 StartZ=0 EndX=-50.8 EndY=24 EndZ=0
    g4: LineSegment StartX=-54.8 StartY=256.6 StartZ=0 EndX=-54.8 EndY=20 EndZ=0
    g5: LineSegment [constr] StartX=-54.8 StartY=20 StartZ=0 EndX=54.8 EndY=20 EndZ=0
    g6: LineSegment StartX=24.8 StartY=185.058 StartZ=0 EndX=-24.8 EndY=185.058 EndZ=0
    g7: LineSegment StartX=-24.8 StartY=185.058 StartZ=0 EndX=-24.8 EndY=179.38 EndZ=0
    g8: LineSegment StartX=-24.8 StartY=179.38 StartZ=0 EndX=24.8 EndY=179.38 EndZ=0
    g9: LineSegment StartX=24.8 StartY=179.38 StartZ=0 EndX=24.8 EndY=185.058 EndZ=0
    g10: LineSegment StartX=24.8 StartY=141.478 StartZ=0 EndX=-24.8 EndY=141.478 EndZ=0
    g11: LineSegment StartX=-24.8 StartY=141.478 StartZ=0 EndX=-24.8 EndY=150.178 EndZ=0
    g12: LineSegment StartX=-24.8 StartY=150.178 StartZ=0 EndX=24.8 EndY=150.178 EndZ=0
    g13: LineSegment StartX=24.8 StartY=150.178 StartZ=0 EndX=24.8 EndY=141.478 EndZ=0
    g14: LineSegment StartX=24.8 StartY=238.453 StartZ=0 EndX=-24.9755 EndY=238.453 EndZ=0
    g15: LineSegment StartX=-24.9755 StartY=238.453 StartZ=0 EndX=-24.9755 EndY=206.288 EndZ=0
    g16: LineSegment StartX=-24.9755 StartY=206.288 StartZ=0 EndX=24.8 EndY=206.288 EndZ=0
    g17: LineSegment StartX=24.8 StartY=206.288 StartZ=0 EndX=24.8 EndY=238.453 EndZ=0
    g18: LineSegment StartX=-24.8 StartY=45.5713 StartZ=0 EndX=-24.8 EndY=29.1792 EndZ=0
    g19: LineSegment StartX=-24.8 StartY=29.1792 StartZ=0 EndX=24.8 EndY=29.1792 EndZ=0
    g20: LineSegment StartX=24.8 StartY=29.1792 StartZ=0 EndX=24.8 EndY=45.5713 EndZ=0
    g21: LineSegment StartX=24.8 StartY=45.5713 StartZ=0 EndX=-24.8 EndY=45.5713 EndZ=0
    g22: LineSegment StartX=-24.8 StartY=15.6864 StartZ=0 EndX=-24.8 EndY=9.07096 EndZ=0
    g23: LineSegment StartX=-24.8 StartY=9.07096 StartZ=0 EndX=24.8 EndY=9.07096 EndZ=0
    g24: LineSegment StartX=24.8 StartY=9.07096 StartZ=0 EndX=24.8 EndY=15.6864 EndZ=0
    g25: LineSegment StartX=24.8 StartY=15.6864 StartZ=0 EndX=-24.8 EndY=15.6864 EndZ=0
    g26: LineSegment StartX=54.8 StartY=20 StartZ=0 EndX=54.8 EndY=256.6 EndZ=0
    g27: LineSegment [constr] StartX=-54.8 StartY=256.6 StartZ=0 EndX=54.8 EndY=256.6 EndZ=0
    g28: LineSegment StartX=-54.8 StartY=20 StartZ=0 EndX=-54.8 EndY=0 EndZ=0
    g29: LineSegment StartX=-54.8 StartY=0 StartZ=0 EndX=54.8 EndY=0 EndZ=0
    g30: LineSegment StartX=54.8 StartY=0 StartZ=0 EndX=54.8 EndY=20 EndZ=0
    g31: LineSegment [constr] StartX=54.8 StartY=20 StartZ=0 EndX=-54.8 EndY=20 EndZ=0
    g32: LineSegment StartX=-54.8 StartY=256.6 StartZ=0 EndX=-54.8 EndY=259 EndZ=0
    g33: LineSegment StartX=-54.8 StartY=259 StartZ=0 EndX=54.8 EndY=259 EndZ=0
    g34: LineSegment StartX=54.8 StartY=259 StartZ=0 EndX=54.8 EndY=256.6 EndZ=0
    g35: Circle CenterX=-44.8 CenterY=30 CenterZ=0 NormalX=0 NormalY=0 NormalZ=1 AngleXU=0 Radius=0.855
    g36: Circle CenterX=44.8 CenterY=30 CenterZ=0 NormalX=0 NormalY=0 NormalZ=1 AngleXU=0 Radius=0.855
    g37: Circle CenterX=-44.8 CenterY=125 CenterZ=0 NormalX=0 NormalY=0 NormalZ=1 AngleXU=0 Radius=0.855
    g38: Circle CenterX=44.8 CenterY=125 CenterZ=0 NormalX=0 NormalY=0 NormalZ=1 AngleXU=0 Radius=0.855
    g39: Circle CenterX=-44.8 CenterY=170 CenterZ=0 NormalX=0 NormalY=0 NormalZ=1 AngleXU=0 Radius=0.855
    g40: Circle CenterX=44.8 CenterY=170 CenterZ=0 NormalX=0 NormalY=0 NormalZ=1 AngleXU=0 Radius=0.855
    g41: Circle CenterX=-44.8 CenterY=145 CenterZ=0 NormalX=0 NormalY=0 NormalZ=1 AngleXU=0 Radius=0.855
    g42: Circle CenterX=44.8 CenterY=145 CenterZ=0 NormalX=0 NormalY=0 NormalZ=1 AngleXU=0 Radius=0.855
    g43: Circle CenterX=-44.8 CenterY=230 CenterZ=0 NormalX=0 NormalY=0 NormalZ=1 AngleXU=0 Radius=0.855
    g44: Circle CenterX=44.8 CenterY=230 CenterZ=0 NormalX=0 NormalY=0 NormalZ=1 AngleXU=0 Radius=0.855
    g45: LineSegment StartX=-24.8 StartY=68.1188 StartZ=0 EndX=24.8 EndY=68.1188 EndZ=0
    g46: LineSegment StartX=24.8 StartY=68.1188 StartZ=0 EndX=24.8 EndY=84.7075 EndZ=0
    g47: LineSegment StartX=24.8 StartY=84.7075 StartZ=0 EndX=-24.8 EndY=84.7075 EndZ=0
    g48: LineSegment StartX=-24.8 StartY=84.7075 StartZ=0 EndX=-24.8 EndY=68.1188 EndZ=0
    g49: Circle CenterX=-44.8 CenterY=104 CenterZ=0 NormalX=0 NormalY=0 NormalZ=1 AngleXU=0 Radius=0.855
    g50: Circle CenterX=44.8 CenterY=104 CenterZ=0 NormalX=0 NormalY=0 NormalZ=1 AngleXU=0 Radius=0.85
    g51: Circle CenterX=26.7285 CenterY=19.305 CenterZ=0 NormalX=0 NormalY=0 NormalZ=1 AngleXU=0 Radius=2
    g52: Circle CenterX=16.7285 CenterY=19.305 CenterZ=0 NormalX=0 NormalY=0 NormalZ=1 AngleXU=0 Radius=2
    g53: Circle CenterX=-36.1991 CenterY=148.72 CenterZ=0 NormalX=0 NormalY=0 NormalZ=1 AngleXU=0 Radius=2
    g54: Circle CenterX=-36.1991 CenterY=138.72 CenterZ=0 NormalX=0 NormalY=0 NormalZ=1 AngleXU=0 Radius=2
    g55: Circle CenterX=37.6894 CenterY=124.612 CenterZ=0 NormalX=0 NormalY=0 NormalZ=1 AngleXU=0 Radius=2
    g56: Circle CenterX=27.6894 CenterY=124.612 CenterZ=0 NormalX=0 NormalY=0 NormalZ=1 AngleXU=0 Radius=2
    g57: Circle CenterX=-19.2979 CenterY=19.305 CenterZ=0 NormalX=0 NormalY=0 NormalZ=1 AngleXU=0 Radius=2
    g58: Circle CenterX=-29.2979 CenterY=19.305 CenterZ=0 NormalX=0 NormalY=0 NormalZ=1 AngleXU=0 Radius=2
    g59: Circle CenterX=4.92244 CenterY=19.305 CenterZ=0 NormalX=0 NormalY=0 NormalZ=1 AngleXU=0 Radius=2
    g60: Circle CenterX=-5.07756 CenterY=19.305 CenterZ=0 NormalX=0 NormalY=0 NormalZ=1 AngleXU=0 Radius=2
    g61: Circle CenterX=-8.62291 CenterY=114.905 CenterZ=0 NormalX=0 NormalY=0 NormalZ=1 AngleXU=0 Radius=2
    g62: Circle CenterX=-18.6229 CenterY=114.905 CenterZ=0 NormalX=0 NormalY=0 NormalZ=1 AngleXU=0 Radius=2
    g63: Circle CenterX=-37.8246 CenterY=197.703 CenterZ=0 NormalX=0 NormalY=0 NormalZ=1 AngleXU=0 Radius=2
    g64: Circle CenterX=-47.8246 CenterY=197.703 CenterZ=0 NormalX=0 NormalY=0 NormalZ=1 AngleXU=0 Radius=2
    g65: Circle CenterX=-39.4472 CenterY=26.999 CenterZ=0 NormalX=0 NormalY=0 NormalZ=1 AngleXU=0 Radius=2
    g66: Circle CenterX=-49.4472 CenterY=26.999 CenterZ=0 NormalX=0 NormalY=0 NormalZ=1 AngleXU=0 Radius=2
    g67: LineSegment StartX=24.8 StartY=174.315 StartZ=0 EndX=-24.8 EndY=174.315 EndZ=0
    g68: LineSegment StartX=-24.8 StartY=174.315 StartZ=0 EndX=-24.8 EndY=165.952 EndZ=0
    g69: LineSegment StartX=-24.8 StartY=165.952 StartZ=0 EndX=24.8 EndY=165.952 EndZ=0
    g70: LineSegment StartX=24.8 StartY=165.952 StartZ=0 EndX=24.8 EndY=174.315 EndZ=0
    g71: LineSegment StartX=-24.8 StartY=89.2998 StartZ=0 EndX=24.8 EndY=89.2998 EndZ=0
    g72: LineSegment StartX=24.8 StartY=89.2998 StartZ=0 EndX=24.8 EndY=101.642 EndZ=0
    g73: LineSegment StartX=24.8 StartY=101.642 StartZ=0 EndX=-24.8 EndY=101.642 EndZ=0
    g74: LineSegment StartX=-24.8 StartY=101.642 StartZ=0 EndX=-24.8 EndY=89.2998 EndZ=0
  constraints (188):
    c: Coincident(g0,g1)
    c: Coincident(g1,g2)
    c: Coincident(g2,g3)
    c: Coincident(g3,g0)
    c: Horizontal(g2)
    c: Vertical(g1)
    c: Vertical(g3)
    c: DistanceY(g0,g2) = 228.6
    c: DistanceX(g0,g0) = 101.6
    c: DistanceX(g0,g-1) = 50.8
    c: Coincident(g4,g5)
    c: Vertical(g4)
    c: Horizontal(g5)
    c: DistanceX(g4,g0) = 4
    c: Horizontal(g0)
    c: Coincident(g6,g7)
    c: Coincident(g7,g8)
    c: Coincident(g8,g9)
    c: Coincident(g9,g6)
    c: Horizontal(g6)
    c: Horizontal(g8)
    c: Vertical(g7)
    c: Vertical(g9)
    c: Coincident(g10,g11)
    c: Coincident(g11,g12)
    c: Coincident(g12,g13)
    c: Coincident(g13,g10)
    c: Horizontal(g10)
    c: Horizontal(g12)
    c: Vertical(g11)
    c: Vertical(g13)
    c: Coincident(g14,g15)
    c: Coincident(g15,g16)
    c: Coincident(g16,g17)
    c: Coincident(g17,g14)
    c: Horizontal(g14)
    c: Horizontal(g16)
    c: Vertical(g15)
    c: Vertical(g17)
    c: Coincident(g18,g19)
    c: Coincident(g19,g20)
    c: Coincident(g20,g21)
    c: Coincident(g21,g18)
    c: Vertical(g18)
    c: Vertical(g20)
    c: Horizontal(g19)
    c: Horizontal(g21)
    c: Coincident(g22,g23)
    c: Coincident(g23,g24)
    c: Coincident(g24,g25)
    c: Coincident(g25,g22)
    c: Vertical(g22)
    c: Vertical(g24)
    c: Horizontal(g23)
    c: Horizontal(g25)
    c: Vertical(g18,g22)
    c: Vertical(g10,g20)
    c: Vertical(g20,g24)
    c: Coincident(g26,g5)
    c: Vertical(g26)
    c: DistanceY(g1,g26) = 4
    c: Horizontal(g4,g26)
    c: Coincident(g27,g4)
    c: Coincident(g27,g26)
    c: DistanceX(g4,g5) = 109.6
    c: DistanceY(g-1,g5) = 20
    c: Coincident(g28,g29)
    c: Coincident(g29,g30)
    c: Coincident(g30,g31)
    c: Coincident(g31,g28)
    c: Vertical(g28)
    c: Vertical(g30)
    c: Horizontal(g29)
    c: Horizontal(g31)
    c: Coincident(g28,g4)
    c: Horizontal(g29,g-1)
    c: Vertical(g30,g5)
    c: Coincident(g32,g4)
    c: Vertical(g32)
    c: Coincident(g33,g32)
    c: Horizontal(g33)
    c: Coincident(g34,g33)
    c: Coincident(g34,g26)
    c: Vertical(g34)
    c: DistanceX(g28,g22) = 30
    c: DistanceX(g23,g29) = 30
    c: Vertical(g10,g18)
    c: Vertical(g11,g7)
    c: Vertical(g12,g8)
    c: DistanceY(g29,g33) = 259
    c: Diameter(g35) = 1.71
    c: Diameter(g36) = 1.71
    c: Horizontal(g36,g35)
    c: DistanceX(g4,g35) = 10
    c: DistanceX(g36,g5) = 10
    c: Diameter(g37) = 1.71
    c: Diameter(g38) = 1.71
    c: Horizontal(g38,g37)
    c: Diameter(g39) = 1.71
    c: Diameter(g40) = 1.71
    c: Horizontal(g40,g39)
    c: Vertical(g39,g35)
    c: Vertical(g40,g38)
    c: Diameter(g41) = 1.71
    c: Diameter(g42) = 1.71
    c: Horizontal(g42,g41)
    c: DistanceY(g-1,g35) = 30
    c: DistanceY(g-1,g37) = 125
    c: Vertical(g41,g37)
    c: DistanceY(g-1,g41) = 145
    c: DistanceY(g-1,g39) = 170
    c: Vertical(g38,g42)
    c: Diameter(g44) = 1.71
    c: Diameter(g43) = 1.71
    c: Vertical(g44,g40)
    c: Vertical(g43,g39)
    c: DistanceY(g-1,g43) = 230
    c: Horizontal(g44,g43)
    c: Coincident(g45,g46)
    c: Coincident(g46,g47)
    c: Coincident(g47,g48)
    c: Coincident(g48,g45)
    c: Horizontal(g45)
    c: Horizontal(g47)
    c: Vertical(g46)
    c: Vertical(g48)
    c: Vertical(g45,g18)
    c: Vertical(g45,g20)
    c: Diameter(g49) = 1.71
    c: Vertical(g37,g49)
    c: Diameter(g50) = 1.7
    c: Horizontal(g49,g50)
    c: Vertical(g50,g38)
    c: DistanceY(g-1,g49) = 104
    c: Diameter(g51) = 4
    c: Diameter(g52) = 4
    c: DistanceY(g54,g53) = 10
    c: Vertical(g54,g53)
    c: Diameter(g53) = 4
    c: Diameter(g54) = 4
    c: Horizontal(g51,g52)
    c: DistanceX(g52,g51) = 10
    c: Diameter(g55) = 4
    c: Diameter(g56) = 4
    c: Horizontal(g55,g56)
    c: DistanceX(g56,g55) = 10
    c: Diameter(g57) = 4
    c: Diameter(g58) = 4
    c: Horizontal(g57,g58)
    c: DistanceX(g58,g57) = 10
    c: Diameter(g59) = 4
    c: Diameter(g60) = 4
    c: Horizontal(g59,g60)
    c: DistanceX(g60,g59) = 10
    c: Diameter(g61) = 4
    c: Diameter(g62) = 4
    c: Horizontal(g61,g62)
    c: DistanceX(g62,g61) = 10
    c: Diameter(g63) = 4
    c: Diameter(g64) = 4
    c: Horizontal(g63,g64)
    c: DistanceX(g64,g63) = 10
    c: Diameter(g65) = 4
    c: Diameter(g66) = 4
    c: Horizontal(g65,g66)
    c: DistanceX(g66,g65) = 10
    c: Horizontal(g57,g60)
    c: Horizontal(g59,g52)
    c: Coincident(g67,g68)
    c: Coincident(g68,g69)
    c: Coincident(g69,g70)
    c: Coincident(g70,g67)
    c: Horizontal(g67)
    c: Horizontal(g69)
    c: Vertical(g68)
    c: Vertical(g70)
    c: Vertical(g68,g7)
    c: Vertical(g69,g8)
    c: Coincident(g71,g72)
    c: Coincident(g72,g73)
    c: Coincident(g73,g74)
    c: Coincident(g74,g71)
    c: Horizontal(g71)
    c: Horizontal(g73)
    c: Vertical(g72)
    c: Vertical(g74)
    c: Vertical(g45,g71)
    c: Vertical(g71,g45)
FEATURE [PartDesign::Pad] Pad004  label="Frontplate Pad"
  Direction = (0,-1,2e-16)
  Length = 3
  Length2 = 10
  Placement = pos=(0,0,0) rot=(1,0,0;1.5708rad)
  Profile = -> Sketch005
  ReferenceAxis = -> Sketch005 [N_Axis]
  Reversed = true
  Suppressed = false
  Type = 0
  expr: Length = <<Monitor Chassis Parameters>>.GSBackPlateThickness
FEATURE [Sketcher::SketchObject] Sketch007  label="Frontplate Foot Sketch"
  ArcFitTolerance = 1e-06
  AttachmentSupport = -> [XZ_Plane002]
  FullyConstrained = true
  MakeInternals = false
  MapMode = 5
  Placement = pos=(0,0,0) rot=(1,0,0;1.5708rad)
  expr: Constraints[11] = <<Monitor Chassis Parameters>>.GSTowerFeetThickness
  expr: Constraints[21] = <<Monitor Chassis Parameters>>.GSTowerFeetThickness
  expr: Constraints[22] = <<Monitor Chassis Parameters>>.GSBackPlateFootWidth
  expr: Constraints[23] = 0.5 * <<Monitor Chassis Parameters>>.GSBackPlateWidth
  expr: Constraints[8] = <<Monitor Chassis Parameters>>.GSBackPlateFootWidth
  expr: Constraints[9] = 0.5 * <<Monitor Chassis Parameters>>.GSBackPlateWidth
  sketch-geometry (8):
    g0: LineSegment StartX=-54.8 StartY=-5 StartZ=0 EndX=-19.8 EndY=-5 EndZ=0
    g1: LineSegment StartX=-19.8 StartY=-5 StartZ=0 EndX=-19.8 EndY=0 EndZ=0
    g2: LineSegment StartX=-19.8 StartY=0 StartZ=0 EndX=-54.8 EndY=0 EndZ=0
    g3: LineSegment StartX=-54.8 StartY=0 StartZ=0 EndX=-54.8 EndY=-5 EndZ=0
    g4: LineSegment StartX=54.8 StartY=-5 StartZ=0 EndX=54.8 EndY=0 EndZ=0
    g5: LineSegment StartX=54.8 StartY=0 StartZ=0 EndX=19.8 EndY=0 EndZ=0
    g6: LineSegment StartX=19.8 StartY=0 StartZ=0 EndX=19.8 EndY=-5 EndZ=0
    g7: LineSegment StartX=19.8 StartY=-5 StartZ=0 EndX=54.8 EndY=-5 EndZ=0
  constraints (24):
    c: Coincident(g0,g1)
    c: Coincident(g1,g2)
    c: Coincident(g2,g3)
    c: Coincident(g3,g0)
    c: Horizontal(g0)
    c: Horizontal(g2)
    c: Vertical(g1)
    c: Vertical(g3)
    c: DistanceX(g2,g1) = 35
    c: DistanceX(g2,g-1) = 54.8
    c: Horizontal(g2,g-1)
    c: DistanceY(g0,g2) = 5
    c: Coincident(g4,g5)
    c: Coincident(g5,g6)
    c: Coincident(g6,g7)
    c: Coincident(g7,g4)
    c: Vertical(g4)
    c: Vertical(g6)
    c: Horizontal(g5)
    c: Horizontal(g7)
    c: Horizontal(g5,g-1)
    c: DistanceY(g4,g4) = 5
    c: DistanceX(g6,g4) = 35
    c: DistanceX(g-1,g4) = 54.8
FEATURE [PartDesign::Pad] Pad006  label="Frontplate Foot Pad"
  BaseFeature = -> Pad004
  Direction = (0,-1,2e-16)
  Length = 65
  Length2 = 3
  Placement = pos=(0,0,0) rot=(1,0,0;1.5708rad)
  Profile = -> Sketch007
  ReferenceAxis = -> Sketch007 [N_Axis]
  Suppressed = false
  Type = 4
  expr: Length = <<Monitor Chassis Parameters>>.GSBackPlateFootLengthForward
  expr: Length2 = <<Monitor Chassis Parameters>>.GSBackPlateThickness
FEATURE [Sketcher::SketchObject] Sketch008  label="Frontplate Foot Screw Holes Sketch"
  ArcFitTolerance = 1e-06
  AttachmentSupport = -> [XY_Plane002]
  FullyConstrained = true
  MakeInternals = false
  MapMode = 5
  expr: Constraints[0] = <<Monitor Chassis Parameters>>.GSBackPlateFootScrewHoleForwardOffset
  expr: Constraints[1] = 0.5 * <<Monitor Chassis Parameters>>.GSBackPlateWidth - 0.5 * <<Monitor Chassis Parameters>>.GSBackPlateFootWidth
  expr: Constraints[2] = 0.5 * <<Monitor Chassis Parameters>>.GSBackPlateWidth - 0.5 * <<Monitor Chassis Parameters>>.GSBackPlateFootWidth
  expr: Constraints[3] = <<Monitor Chassis Parameters>>.GSTowerFeetScrewDiameter
  expr: Constraints[4] = <<Monitor Chassis Parameters>>.GSTowerFeetScrewDiameter
  sketch-geometry (2):
    g0: Circle CenterX=-37.3 CenterY=-59 CenterZ=0 NormalX=0 NormalY=0 NormalZ=1 AngleXU=0 Radius=1.7
    g1: Circle CenterX=37.3 CenterY=-59 CenterZ=0 NormalX=0 NormalY=0 NormalZ=1 AngleXU=0 Radius=1.7
  constraints (6):
    c: DistanceY(g0,g-1) = 59
    c: DistanceX(g0,g-1) = 37.3
    c: DistanceX(g-1,g1) = 37.3
    c: Diameter(g0) = 3.4
    c: Diameter(g1) = 3.4
    c: Horizontal(g1,g0)
FEATURE [PartDesign::Hole] Hole001  label="Frontplate Foot Screw Holes"
  BaseFeature = -> Pad006
  CustomThreadClearance = 0
  Depth = 25
  DepthType = 0
  Diameter = 3.4
  DrillForDepth = false
  DrillPoint = 1
  DrillPointAngle = 118
  HoleCutCountersinkAngle = 90
  HoleCutCustomValues = false
  HoleCutDepth = 0
  HoleCutDiameter = 8
  HoleCutType = 2
  ModelThread = false
  Placement = pos=(0,0,0) rot=(1,0,0;1.5708rad)
  Profile = -> Sketch008
  Suppressed = false
  Tapered = false
  TaperedAngle = 90
  ThreadClass = 0
  ThreadDepth = 25
  ThreadDepthType = 0
  ThreadDirection = 0
  ThreadFit = 0
  ThreadSize = 0
  ThreadType = 0
  Threaded = false
  UseCustomThreadClearance = false
  expr: Diameter = <<Monitor Chassis Parameters>>.GSTowerFeetScrewDiameter
  expr: HoleCutDiameter = <<Monitor Chassis Parameters>>.GSM4BoltCountersinkDiameter
FEATURE [Sketcher::SketchObject] Sketch009  label="Frontplate Foot Support Corner Sketch"
  ArcFitTolerance = 1e-06
  AttachmentSupport = -> [DatumPlane001]
  FullyConstrained = true
  MakeInternals = false
  MapMode = 5
  Placement = pos=(54.8,0,0) rot=(0.57735,0.57735,0.57735;2.0944rad)
  expr: Constraints[1] = <<Monitor Chassis Parameters>>.GSBackPlateThickness
  expr: Constraints[24] = 0.8 * <<Monitor Chassis Parameters>>.GSTowerFloorDepth
  expr: Constraints[25] = 0.6 * <<Monitor Chassis Parameters>>.GSTowerFloorDepth
  expr: Constraints[26] = <<Monitor Chassis Parameters>>.GSSideCornerCutoutInset
  expr: Constraints[27] = <<Monitor Chassis Parameters>>.GSSideCornerCutoutInset
  expr: Constraints[28] = 2 * <<Monitor Chassis Parameters>>.GSSideCornerCutoutInset
  expr: Constraints[29] = 3 * <<Monitor Chassis Parameters>>.GSSideCornerCutoutInset
  expr: Constraints[39] = 0.8 * <<Monitor Chassis Parameters>>.GSTowerFloorDepth
  expr: Constraints[3] = <<Monitor Chassis Parameters>>.GSTowerFeetThickness
  expr: Constraints[41] = <<Monitor Chassis Parameters>>.GSSideCornerCutoutInset
  expr: Constraints[42] = -2 * <<Monitor Chassis Parameters>>.GSSideCornerCutoutInset
  expr: Constraints[43] = 3 * <<Monitor Chassis Parameters>>.GSSideCornerCutoutInset
  expr: Constraints[54] = 0.8 * <<Monitor Chassis Parameters>>.GSTowerFloorDepth
  expr: Constraints[55] = 0.6 * <<Monitor Chassis Parameters>>.GSTowerFloorDepth
  expr: Constraints[56] = <<Monitor Chassis Parameters>>.GSSideCornerCutoutInset
  expr: Constraints[57] = <<Monitor Chassis Parameters>>.GSSideCornerCutoutInset
  expr: Constraints[58] = 2 * <<Monitor Chassis Parameters>>.GSSideCornerCutoutInset
  expr: Constraints[59] = 3 * <<Monitor Chassis Parameters>>.GSSideCornerCutoutInset
  expr: Constraints[62] = <<Monitor Chassis Parameters>>.GSTowerThirdFloorHeight
  expr: Constraints[63] = <<Monitor Chassis Parameters>>.GSTowerSecondFloorHeight
  expr: Constraints[64] = 0.6 * <<Monitor Chassis Parameters>>.GSTowerFloorDepth
  expr: Constraints[65] = <<Monitor Chassis Parameters>>.GSTowerFourthFloorHeight + <<Monitor Chassis Parameters>>.GSTowerFloorThickness
  expr: Constraints[6] = 0.8 * <<Monitor Chassis Parameters>>.GSTowerFloorDepth
  expr: Constraints[70] = 2 * <<Monitor Chassis Parameters>>.GSSideCornerCutoutInset
  expr: Constraints[71] = 3 * <<Monitor Chassis Parameters>>.GSSideCornerCutoutInset
  expr: Constraints[73] = <<Monitor Chassis Parameters>>.GSSideCornerCutoutInset
  expr: Constraints[7] = 0.6 * <<Monitor Chassis Parameters>>.GSTowerFloorDepth
  sketch-geometry (24):
    g0: LineSegment StartX=-41 StartY=-5 StartZ=0 EndX=3 EndY=-5 EndZ=0
    g1: LineSegment StartX=3 StartY=28 StartZ=0 EndX=3 EndY=-5 EndZ=0
    g2: LineSegment StartX=-41 StartY=-5 StartZ=0 EndX=3 EndY=28 EndZ=0
    g3: LineSegment StartX=-23 StartY=181 StartZ=0 EndX=-3 EndY=196 EndZ=0
    g4: LineSegment StartX=-3 StartY=196 StartZ=0 EndX=-3 EndY=181 EndZ=0
    g5: LineSegment StartX=-23 StartY=181 StartZ=0 EndX=-3 EndY=181 EndZ=0
    g6: LineSegment StartX=3 StartY=208 StartZ=0 EndX=3 EndY=175 EndZ=0
    g7: LineSegment StartX=3 StartY=175 StartZ=0 EndX=-41 EndY=175 EndZ=0
    g8: LineSegment StartX=-41 StartY=175 StartZ=0 EndX=3 EndY=208 EndZ=0
    g9: LineSegment StartX=-23 StartY=1 StartZ=0 EndX=-3 EndY=16 EndZ=0
    g10: LineSegment StartX=-3 StartY=16 StartZ=0 EndX=-3 EndY=1 EndZ=0
    g11: LineSegment StartX=-23 StartY=1 StartZ=0 EndX=-3 EndY=1 EndZ=0
    g12: LineSegment StartX=-23 StartY=253 StartZ=0 EndX=-3 EndY=238 EndZ=0
    g13: LineSegment StartX=-3 StartY=238 StartZ=0 EndX=-3 EndY=253 EndZ=0
    g14: LineSegment StartX=-23 StartY=253 StartZ=0 EndX=-3 EndY=253 EndZ=0
    g15: LineSegment StartX=3 StartY=226 StartZ=0 EndX=3 EndY=259 EndZ=0
    g16: LineSegment StartX=3 StartY=259 StartZ=0 EndX=-41 EndY=259 EndZ=0
    g17: LineSegment StartX=-41 StartY=259 StartZ=0 EndX=3 EndY=226 EndZ=0
    g18: LineSegment StartX=-23 StartY=91 StartZ=0 EndX=-3 EndY=106 EndZ=0
    g19: LineSegment StartX=-3 StartY=106 StartZ=0 EndX=-3 EndY=91 EndZ=0
    g20: LineSegment StartX=-23 StartY=91 StartZ=0 EndX=-3 EndY=91 EndZ=0
    g21: LineSegment StartX=3 StartY=118 StartZ=0 EndX=3 EndY=85 EndZ=0
    g22: LineSegment StartX=3 StartY=85 StartZ=0 EndX=-41 EndY=85 EndZ=0
    g23: LineSegment StartX=-41 StartY=85 StartZ=0 EndX=3 EndY=118 EndZ=0
  constraints (74):
    c: Horizontal(g0)
    c: DistanceX(g-1,g0) = 3
    c: Vertical(g1)
    c: DistanceY(g0,g-1) = 5
    c: Coincident(g2,g0)
    c: Coincident(g2,g1)
    c: DistanceX(g0,g0) = 44
    c: DistanceY(g0,g1) = 33
    c: Coincident(g4,g3)
    c: Vertical(g4)
    c: Coincident(g5,g3)
    c: Coincident(g5,g4)
    c: Horizontal(g5)
    c: Vertical(g6)
    c: Coincident(g7,g6)
    c: Horizontal(g7)
    c: Coincident(g8,g7)
    c: Coincident(g8,g6)
    c: Coincident(g10,g9)
    c: Vertical(g10)
    c: Coincident(g11,g9)
    c: Coincident(g11,g10)
    c: Horizontal(g11)
    c: Vertical(g6,g1)
    c: DistanceX(g7,g6) = 44
    c: DistanceY(g6,g6) = 33
    c: DistanceY(g6,g4) = 6
    c: DistanceX(g4,g6) = 6
    c: DistanceY(g3,g6) = 12
    c: DistanceX(g7,g3) = 18
    c: Coincident(g13,g12)
    c: Vertical(g13)
    c: Coincident(g14,g12)
    c: Coincident(g14,g13)
    c: Horizontal(g14)
    c: Vertical(g15)
    c: Horizontal(g16)
    c: Coincident(g17,g16)
    c: Coincident(g17,g15)
    c: DistanceX(g16,g15) = 44
    c: DistanceY(g15,g13) = -6
    c: DistanceX(g13,g15) = 6
    c: DistanceY(g12,g15) = -12
    c: DistanceX(g16,g12) = 18
    c: Coincident(g19,g18)
    c: Vertical(g19)
    c: Coincident(g20,g18)
    c: Coincident(g20,g19)
    c: Horizontal(g20)
    c: Vertical(g21)
    c: Coincident(g22,g21)
    c: Horizontal(g22)
    c: Coincident(g23,g22)
    c: Coincident(g23,g21)
    c: DistanceX(g22,g21) = 44
    c: DistanceY(g21,g21) = 33
    c: DistanceY(g21,g19) = 6
    c: DistanceX(g19,g21) = 6
    c: DistanceY(g18,g21) = 12
    c: DistanceX(g22,g18) = 18
    c: Vertical(g21,g6)
    c: Vertical(g6,g15)
    c: DistanceY(g-1,g6) = 175
    c: DistanceY(g-1,g21) = 85
    c: DistanceY(g15,g15) = 33
    c: DistanceY(g-1,g15) = 259
    c: Horizontal(g16,g15)
    c: Vertical(g16,g15)
    c: Vertical(g1,g0)
    c: Horizontal(g1,g0)
    c: DistanceY(g9,g1) = 12
    c: DistanceX(g0,g9) = 18
    c: Vertical(g19,g9)
    c: DistanceY(g0,g10) = 6
FEATURE [PartDesign::Pad] Pad007  label="Frontplate Floor Support Corner Pad"
  BaseFeature = -> Hole001
  Direction = (1,0,0)
  Length = 2.5
  Length2 = 10
  Placement = pos=(0,0,0) rot=(1,0,0;1.5708rad)
  Profile = -> Sketch009
  ReferenceAxis = -> Sketch009 [N_Axis]
  Suppressed = false
  Type = 0
  expr: Length = <<Monitor Chassis Parameters>>.GSSideCornerThickness
FEATURE [PartDesign::Mirrored] Mirrored001  label="Frontplate Floor Support Corner Mirrored"
  BaseFeature = -> Pad007
  MirrorPlane = -> YZ_Plane002
  Originals = -> [Pad007]
  Placement = pos=(0,0,0) rot=(1,0,0;1.5708rad)
  Suppressed = false
  TransformMode = 0
FEATURE [Sketcher::SketchObject] Sketch010  label="Frontplate Floors Sketch"
  ArcFitTolerance = 1e-06
  AttachmentSupport = -> [DatumPlane001]
  FullyConstrained = true
  MakeInternals = false
  MapMode = 5
  Placement = pos=(54.8,0,0) rot=(0.57735,0.57735,0.57735;2.0944rad)
  expr: Constraints[10] = <<Monitor Chassis Parameters>>.GSTowerSecondFloorDepth
  expr: Constraints[21] = <<Monitor Chassis Parameters>>.GSTowerFourthFloorDepth
  expr: Constraints[32] = <<Monitor Chassis Parameters>>.GSTowerThirdFloorDepth
  expr: Constraints[43] = <<Monitor Chassis Parameters>>.GSTowerFirstFloorDepth
  expr: Constraints[44] = <<Monitor Chassis Parameters>>.GSTowerFirstFloorHeight
  expr: Constraints[45] = <<Monitor Chassis Parameters>>.GSTowerSecondFloorHeight
  expr: Constraints[46] = <<Monitor Chassis Parameters>>.GSTowerFourthFloorHeight
  expr: Constraints[47] = <<Monitor Chassis Parameters>>.GSTowerThirdFloorHeight
  expr: Constraints[9] = <<Monitor Chassis Parameters>>.GSTowerFloorThickness
  sketch-geometry (16):
    g0: LineSegment StartX=-55 StartY=85 StartZ=0 EndX=0 EndY=85 EndZ=0
    g1: LineSegment StartX=0 StartY=85 StartZ=0 EndX=0 EndY=89 EndZ=0
    g2: LineSegment StartX=0 StartY=89 StartZ=0 EndX=-55 EndY=89 EndZ=0
    g3: LineSegment StartX=-55 StartY=89 StartZ=0 EndX=-55 EndY=85 EndZ=0
    g4: LineSegment StartX=-55 StartY=255 StartZ=0 EndX=0 EndY=255 EndZ=0
    g5: LineSegment StartX=0 StartY=255 StartZ=0 EndX=0 EndY=259 EndZ=0
    g6: LineSegment StartX=0 StartY=259 StartZ=0 EndX=-55 EndY=259 EndZ=0
    g7: LineSegment StartX=-55 StartY=259 StartZ=0 EndX=-55 EndY=255 EndZ=0
    g8: LineSegment StartX=-55 StartY=175 StartZ=0 EndX=0 EndY=175 EndZ=0
    g9: LineSegment StartX=0 StartY=175 StartZ=0 EndX=0 EndY=179 EndZ=0
    g10: LineSegment StartX=0 StartY=179 StartZ=0 EndX=-55 EndY=179 EndZ=0
    g11: LineSegment StartX=-55 StartY=179 StartZ=0 EndX=-55 EndY=175 EndZ=0
    g12: LineSegment StartX=-50 StartY=5 StartZ=0 EndX=0 EndY=5 EndZ=0
    g13: LineSegment StartX=0 StartY=5 StartZ=0 EndX=0 EndY=9 EndZ=0
    g14: LineSegment StartX=0 StartY=9 StartZ=0 EndX=-50 EndY=9 EndZ=0
    g15: LineSegment StartX=-50 StartY=9 StartZ=0 EndX=-50 EndY=5 EndZ=0
  constraints (48):
    c: Coincident(g0,g1)
    c: Coincident(g1,g2)
    c: Coincident(g2,g3)
    c: Coincident(g3,g0)
    c: Horizontal(g0)
    c: Horizontal(g2)
    c: Vertical(g1)
    c: Vertical(g3)
    c: Vertical(g0,g-1)
    c: DistanceY(g0,g2) = 4
    c: DistanceX(g2,g1) = 55
    c: Coincident(g4,g5)
    c: Coincident(g5,g6)
    c: Coincident(g6,g7)
    c: Coincident(g7,g4)
    c: Horizontal(g4)
    c: Horizontal(g6)
    c: Vertical(g5)
    c: Vertical(g7)
    c: Vertical(g4,g-1)
    c: DistanceY(g4,g6) = 4
    c: DistanceX(g6,g5) = 55
    c: Coincident(g8,g9)
    c: Coincident(g9,g10)
    c: Coincident(g10,g11)
    c: Coincident(g11,g8)
    c: Horizontal(g8)
    c: Horizontal(g10)
    c: Vertical(g9)
    c: Vertical(g11)
    c: Vertical(g8,g-1)
    c: DistanceY(g8,g10) = 4
    c: DistanceX(g10,g9) = 55
    c: Coincident(g12,g13)
    c: Coincident(g13,g14)
    c: Coincident(g14,g15)
    c: Coincident(g15,g12)
    c: Horizontal(g12)
    c: Horizontal(g14)
    c: Vertical(g13)
    c: Vertical(g15)
    c: Vertical(g12,g-1)
    c: DistanceY(g12,g14) = 4
    c: DistanceX(g14,g13) = 50
    c: DistanceY(g-1,g12) = 5
    c: DistanceY(g-1,g0) = 85
    c: DistanceY(g-1,g4) = 255
    c: DistanceY(g-1,g8) = 175
FEATURE [PartDesign::Pad] Pad008  label="Tower Floors Pad"
  BaseFeature = -> Mirrored001
  Direction = (1,0,0)
  Length = 109.6
  Length2 = 10
  Placement = pos=(0,0,0) rot=(1,0,0;1.5708rad)
  Profile = -> Sketch010
  ReferenceAxis = -> Sketch010 [N_Axis]
  Reversed = true
  Suppressed = false
  Type = 0
  expr: Length = <<Monitor Chassis Parameters>>.GSBackPlateWidth
FEATURE [PartDesign::Plane] DatumPlane002  label="First Floor DatumPlane"
  AttachmentOffset = pos=(0,0,9) rot=(0,0,1;0rad)
  AttachmentSupport = -> [XY_Plane002]
  Length = 61.1129
  MapMode = 5
  Placement = pos=(0,0,9) rot=(0,0,1;0rad)
  ResizeMode = 0
  Width = 72.8606
  expr: .AttachmentOffset.Base.z = <<Monitor Chassis Parameters>>.GSTowerFirstFloorHeight + <<Monitor Chassis Parameters>>.GSTowerFloorThickness
FEATURE [PartDesign::Plane] DatumPlane003  label="Second Floor DatumPlane"
  AttachmentOffset = pos=(0,0,89) rot=(0,0,1;0rad)
  AttachmentSupport = -> [XY_Plane002]
  Length = 61.1129
  MapMode = 5
  Placement = pos=(0,0,89) rot=(0,0,1;0rad)
  ResizeMode = 0
  Width = 72.8606
  expr: .AttachmentOffset.Base.z = <<Monitor Chassis Parameters>>.GSTowerSecondFloorHeight + <<Monitor Chassis Parameters>>.GSTowerFloorThickness
FEATURE [PartDesign::Plane] DatumPlane004  label="Third Floor DatumPlane"
  AttachmentOffset = pos=(0,0,179) rot=(0,0,1;0rad)
  AttachmentSupport = -> [XY_Plane002]
  Length = 61.1129
  MapMode = 5
  Placement = pos=(0,0,179) rot=(0,0,1;0rad)
  ResizeMode = 0
  Width = 72.8606
  expr: .AttachmentOffset.Base.z = <<Monitor Chassis Parameters>>.GSTowerThirdFloorHeight + <<Monitor Chassis Parameters>>.GSTowerFloorThickness
FEATURE [Sketcher::SketchObject] Sketch011  label="Third Floor Holes Sketch"
  ArcFitTolerance = 1e-06
  AttachmentSupport = -> [DatumPlane004]
  FullyConstrained = true
  MakeInternals = false
  MapMode = 5
  Placement = pos=(0,0,179) rot=(0,0,1;0rad)
  expr: Constraints[1] = 2 + 0.5 * <<Monitor Chassis Parameters>>.GSTowerThirdFloorDepth
  expr: Constraints[2] = <<Monitor Chassis Parameters>>.GSMonitorFloorCameraMountHoleDiameter
  sketch-geometry (1):
    g0: Circle CenterX=0 CenterY=-29.5 CenterZ=0 NormalX=0 NormalY=0 NormalZ=1 AngleXU=0 Radius=2.75
  constraints (3):
    c: PointOnObject(g0,g-2)
    c: DistanceY(g0,g-1) = 29.5
    c: Diameter(g0) = 5.5
FEATURE [PartDesign::Pocket] Pocket  label="Third Floor Holes Pocket"
  BaseFeature = -> Pad008
  Direction = (0,0,-1)
  Length = 5
  Length2 = 5
  Placement = pos=(0,0,0) rot=(1,0,0;1.5708rad)
  Profile = -> Sketch011
  ReferenceAxis = -> Sketch011 [N_Axis]
  Suppressed = false
  Type = 0
FEATURE [Sketcher::SketchObject] Sketch012  label="Second Floor Holes Sketch"
  ArcFitTolerance = 1e-06
  AttachmentSupport = -> [DatumPlane003]
  FullyConstrained = true
  MakeInternals = false
  MapMode = 2
  Placement = pos=(0,0,89) rot=(0,0,1;0rad)
  expr: Constraints[0] = <<Monitor Chassis Parameters>>.GSMonitorFloorCameraMountHoleDiameter
  expr: Constraints[2] = 12 + 0.4 * <<Monitor Chassis Parameters>>.GSTowerSecondFloorDepth
  sketch-geometry (1):
    g0: Circle CenterX=0 CenterY=-34 CenterZ=0 NormalX=0 NormalY=0 NormalZ=1 AngleXU=0 Radius=2.75
  constraints (3):
    c: Diameter(g0) = 5.5
    c: Vertical(g-1,g0)
    c: DistanceY(g0,g-1) = 34
FEATURE [PartDesign::Pocket] Pocket001  label="Second Floor Holes Pocket"
  BaseFeature = -> Pocket
  Direction = (0,0,-1)
  Length = 5
  Length2 = 5
  Placement = pos=(0,0,0) rot=(1,0,0;1.5708rad)
  Profile = -> Sketch012
  ReferenceAxis = -> Sketch012 [N_Axis]
  Suppressed = false
  Type = 0
FEATURE [Sketcher::SketchObject] Sketch013  label="First Floor Holes Sketch"
  ArcFitTolerance = 1e-06
  AttachmentSupport = -> [DatumPlane002]
  FullyConstrained = true
  MakeInternals = false
  MapMode = 5
  Placement = pos=(0,0,9) rot=(0,0,1;0rad)
  expr: Constraints[0] = <<Monitor Chassis Parameters>>.GSMonitorFloorCameraMountHoleDiameter
  expr: Constraints[2] = 0.5 * <<Monitor Chassis Parameters>>.GSTowerFirstFloorDepth
  sketch-geometry (1):
    g0: Circle CenterX=0 CenterY=-25 CenterZ=0 NormalX=0 NormalY=0 NormalZ=1 AngleXU=0 Radius=2.75
  constraints (3):
    c: Diameter(g0) = 5.5
    c: Vertical(g0,g-1)
    c: DistanceY(g0,g-1) = 25
FEATURE [PartDesign::Pocket] Pocket002  label="First Floor Holes Pocket"
  BaseFeature = -> Pocket001
  Direction = (0,0,-1)
  Length = 5
  Length2 = 5
  Placement = pos=(0,0,0) rot=(1,0,0;1.5708rad)
  Profile = -> Sketch013
  ReferenceAxis = -> Sketch013 [N_Axis]
  Suppressed = false
  Type = 0
FEATURE [Sketcher::SketchObject] Sketch014  label="Shank Shield Riser Sketch"
  ArcFitTolerance = 1e-06
  AttachmentSupport = -> [XZ_Plane002]
  FullyConstrained = true
  MakeInternals = false
  MapMode = 5
  Placement = pos=(0,0,0) rot=(1,0,0;1.5708rad)
  expr: Constraints[0] = 3 * <<Monitor Chassis Parameters>>.GSM4TappingScrewHoleDiameter
  expr: Constraints[1] = <<Monitor Chassis Parameters>>.GSTowerFourthFloorHeight - 1.5 * <<Monitor Chassis Parameters>>.GSM4TappingScrewHoleDiameter
  expr: Constraints[2] = 0.5 * <<Monitor Chassis Parameters>>.GSBackPlateWidth - 1.5 * <<Monitor Chassis Parameters>>.GSM4TappingScrewHoleDiameter
  expr: Constraints[3] = 3 * <<Monitor Chassis Parameters>>.GSM4TappingScrewHoleDiameter
  expr: Constraints[5] = <<Monitor Chassis Parameters>>.GSBackPlateWidth - 3 * <<Monitor Chassis Parameters>>.GSM4TappingScrewHoleDiameter
  sketch-geometry (2):
    g0: Circle CenterX=-49.7 CenterY=249.9 CenterZ=0 NormalX=0 NormalY=0 NormalZ=1 AngleXU=0 Radius=5.1
    g1: Circle CenterX=49.7 CenterY=249.9 CenterZ=0 NormalX=0 NormalY=0 NormalZ=1 AngleXU=0 Radius=5.1
  constraints (6):
    c: Diameter(g0) = 10.2
    c: DistanceY(g-1,g0) = 249.9
    c: DistanceX(g0,g-1) = 49.7
    c: Diameter(g1) = 10.2
    c: Horizontal(g0,g1)
    c: DistanceX(g0,g1) = 99.4
FEATURE [PartDesign::Pad] Pad009  label="Shank Shield Riser Pad"
  BaseFeature = -> Pocket002
  Direction = (0,-1,2e-16)
  Length = 89.65
  Length2 = 10
  Placement = pos=(0,0,0) rot=(1,0,0;1.5708rad)
  Profile = -> Sketch014
  ReferenceAxis = -> Sketch014 [N_Axis]
  Suppressed = false
  Type = 0
  expr: Length = 1 + <<Monitor Chassis Parameters>>.GSBasePowerBoxTowerBackOffsetFromFront - <<Monitor Chassis Parameters>>.GSShankShieldThickness - <<Monitor Chassis Parameters>>.GSBackPlateThickness - 3 * <<Monitor Chassis Parameters>>.GSBasePowerBoxSideThickness
FEATURE [PartDesign::Plane] DatumPlane005  label="Shank Shield Riser Front DatumPlane005"
  AttachmentSupport = -> [Pad009]
  Length = 68.9737
  MapMode = 5
  Placement = pos=(0,-89.65,0) rot=(1,0,0;1.5708rad)
  ResizeMode = 0
  Width = 198.974
FEATURE [Sketcher::SketchObject] Sketch015  label="Shank Shield Riser Screw Holes Sketch"
  ArcFitTolerance = 1e-06
  AttachmentSupport = -> [DatumPlane005]
  FullyConstrained = true
  MakeInternals = false
  MapMode = 5
  Placement = pos=(0,-89.65,0) rot=(1,0,0;1.5708rad)
  expr: Constraints[0] = 0.5 * <<Monitor Chassis Parameters>>.GSBackPlateWidth - 1.5 * <<Monitor Chassis Parameters>>.GSM4TappingScrewHoleDiameter
  expr: Constraints[1] = <<Monitor Chassis Parameters>>.GSM4TappingScrewHoleDiameter
  expr: Constraints[3] = <<Monitor Chassis Parameters>>.GSTowerFourthFloorHeight - 1.5 * <<Monitor Chassis Parameters>>.GSM4TappingScrewHoleDiameter
  expr: Constraints[4] = 0.5 * <<Monitor Chassis Parameters>>.GSBackPlateWidth - 1.5 * <<Monitor Chassis Parameters>>.GSM4TappingScrewHoleDiameter
  expr: Constraints[5] = <<Monitor Chassis Parameters>>.GSM4TappingScrewHoleDiameter
  sketch-geometry (2):
    g0: Circle CenterX=-49.7 CenterY=249.9 CenterZ=0 NormalX=0 NormalY=0 NormalZ=1 AngleXU=0 Radius=1.7
    g1: Circle CenterX=49.7 CenterY=249.9 CenterZ=0 NormalX=0 NormalY=0 NormalZ=1 AngleXU=0 Radius=1.7
  constraints (6):
    c: DistanceX(g0,g-1) = 49.7
    c: Diameter(g0) = 3.4
    c: Horizontal(g0,g1)
    c: DistanceY(g-1,g0) = 249.9
    c: DistanceX(g-1,g1) = 49.7
    c: Diameter(g1) = 3.4
FEATURE [PartDesign::Pocket] Pocket003  label="Shank Shield Riser Screw Holes Pocket"
  BaseFeature = -> Pad009
  Direction = (0,1,-2e-16)
  Length = 14
  Length2 = 5
  Placement = pos=(0,0,0) rot=(1,0,0;1.5708rad)
  Profile = -> Sketch015
  ReferenceAxis = -> Sketch015 [N_Axis]
  Suppressed = false
  Type = 0
  expr: Length = 14
FEATURE [PartDesign::Plane] DatumPlane006  label="Fourth Floor DatumPlane"
  AttachmentOffset = pos=(0,0,259) rot=(0,0,1;0rad)
  AttachmentSupport = -> [XY_Plane002]
  Length = 61.1129
  MapMode = 5
  Placement = pos=(0,0,259) rot=(0,0,1;0rad)
  ResizeMode = 0
  Width = 72.8606
  expr: .AttachmentOffset.Base.z = <<Monitor Chassis Parameters>>.GSTowerFourthFloorHeight + <<Monitor Chassis Parameters>>.GSTowerFloorThickness
FEATURE [Sketcher::SketchObject] Sketch016  label="Fourth Floor Cutout Sketch"
  ArcFitTolerance = 1e-06
  AttachmentSupport = -> [DatumPlane006]
  FullyConstrained = false
  MakeInternals = false
  MapMode = 5
  Placement = pos=(0,0,259) rot=(0,0,1;0rad)
  sketch-geometry (4):
    g0: LineSegment StartX=-44.9421 StartY=-8.20433 StartZ=0 EndX=-44.9421 EndY=-45.1974 EndZ=0
    g1: LineSegment StartX=-44.9421 StartY=-45.1974 StartZ=0 EndX=49.6477 EndY=-45.1974 EndZ=0
    g2: LineSegment StartX=49.6477 StartY=-45.1974 StartZ=0 EndX=49.6477 EndY=-8.20433 EndZ=0
    g3: LineSegment StartX=49.6477 StartY=-8.20433 StartZ=0 EndX=-44.9421 EndY=-8.20433 EndZ=0
  constraints (8):
    c: Coincident(g0,g1)
    c: Coincident(g1,g2)
    c: Coincident(g2,g3)
    c: Coincident(g3,g0)
    c: Vertical(g0)
    c: Vertical(g2)
    c: Horizontal(g1)
    c: Horizontal(g3)
FEATURE [PartDesign::Plane] DatumPlane007  label="Suggested Backplate Split DatumPlane"
  AttachmentOffset = pos=(0,0,120) rot=(0,0,1;0rad)
  AttachmentSupport = -> [XY_Plane001]
  Length = 119.016
  MapMode = 5
  Placement = pos=(0,0,120) rot=(0,0,1;0rad)
  ResizeMode = 0
  Width = 67.0538
  expr: .AttachmentOffset.Base.z = 120
FEATURE [PartDesign::Plane] DatumPlane008  label="Suggested Frontplate Split DatumPlane"
  AttachmentOffset = pos=(0,0,155) rot=(0,0,1;0rad)
  AttachmentSupport = -> [XY_Plane002]
  Length = 61.1129
  MapMode = 5
  Placement = pos=(0,0,155) rot=(0,0,1;0rad)
  ResizeMode = 0
  Width = 72.8606
  expr: .AttachmentOffset.Base.z = 155
FEATURE [PartDesign::Body] Body001  label="Frontplate Body"
  AllowCompound = false
  Group = -> [Sketch005,Pad004,Sketch007,Pad006,Sketch008,Hole001,DatumPlane001,Sketch009,Pad007,Mirrored001,Sketch010,Pad008,DatumPlane002,DatumPlane003,DatumPlane004,Sketch011,Pocket,Sketch012,Pocket001,Sketch013,Pocket002,Sketch014,Pad009,DatumPlane005,Sketch015,Pocket003,DatumPlane006,Sketch016,DatumPlane008]
  Origin = -> Origin002
  Placement = pos=(0.1,5,0) rot=(0,0,1;3.14159rad)
  Tip = -> Pocket003
FEATURE [Sketcher::SketchObject] Sketch017  label="Tower Layer Join Screw Holes Sketch"
  ArcFitTolerance = 1e-06
  AttachmentSupport = -> [XZ_Plane001]
  FullyConstrained = true
  MakeInternals = false
  MapMode = 5
  Placement = pos=(0,0,0) rot=(1,0,0;1.5708rad)
  expr: Constraints[0] = <<Monitor Chassis Parameters>>.GSTowerLayerJoinScrewDiameter
  expr: Constraints[1] = <<Monitor Chassis Parameters>>.GSM2TappingScrewHoleDiameter
  expr: Constraints[22] = 0.5 * <<Monitor Chassis Parameters>>.GSBackPlateWidth - <<Monitor Chassis Parameters>>.GSTowerLayerJoinScrewInset
  expr: Constraints[23] = 0.5 * <<Monitor Chassis Parameters>>.GSBackPlateWidth - <<Monitor Chassis Parameters>>.GSTowerLayerJoinScrewInset
  expr: Constraints[24] = <<Monitor Chassis Parameters>>.GSTowerLayerJoinScrewHeightFromFoot_1
  expr: Constraints[25] = <<Monitor Chassis Parameters>>.GSTowerLayerJoinScrewHeightFromFoot_2
  expr: Constraints[26] = <<Monitor Chassis Parameters>>.GSTowerLayerJoinScrewHeightFromFoot_3
  expr: Constraints[27] = <<Monitor Chassis Parameters>>.GSTowerLayerJoinScrewHeightFromFoot_4
  expr: Constraints[28] = <<Monitor Chassis Parameters>>.GSTowerLayerJoinScrewHeightFromFoot_5
  expr: Constraints[29] = <<Monitor Chassis Parameters>>.GSM2TappingScrewHoleDiameter
  expr: Constraints[2] = <<Monitor Chassis Parameters>>.GSM2TappingScrewHoleDiameter
  expr: Constraints[30] = <<Monitor Chassis Parameters>>.GSM2TappingScrewHoleDiameter
  expr: Constraints[35] = <<Monitor Chassis Parameters>>.GSTowerLayerJoinScrewHeightFromFoot_6
  expr: Constraints[3] = <<Monitor Chassis Parameters>>.GSM2TappingScrewHoleDiameter
  expr: Constraints[4] = <<Monitor Chassis Parameters>>.GSM2TappingScrewHoleDiameter
  expr: Constraints[5] = <<Monitor Chassis Parameters>>.GSM2TappingScrewHoleDiameter
  expr: Constraints[6] = <<Monitor Chassis Parameters>>.GSM2TappingScrewHoleDiameter
  expr: Constraints[7] = <<Monitor Chassis Parameters>>.GSM2TappingScrewHoleDiameter
  expr: Constraints[8] = <<Monitor Chassis Parameters>>.GSM2TappingScrewHoleDiameter
  expr: Constraints[9] = <<Monitor Chassis Parameters>>.GSM2TappingScrewHoleDiameter
  sketch-geometry (12):
    g0: Circle CenterX=44.8 CenterY=170 CenterZ=0 NormalX=0 NormalY=0 NormalZ=1 AngleXU=0 Radius=0.855
    g1: Circle CenterX=-44.8 CenterY=145 CenterZ=0 NormalX=0 NormalY=0 NormalZ=1 AngleXU=0 Radius=0.855
    g2: Circle CenterX=44.8 CenterY=145 CenterZ=0 NormalX=0 NormalY=0 NormalZ=1 AngleXU=0 Radius=0.855
    g3: Circle CenterX=-44.8 CenterY=125 CenterZ=0 NormalX=0 NormalY=0 NormalZ=1 AngleXU=0 Radius=0.855
    g4: Circle CenterX=-44.8 CenterY=104 CenterZ=0 NormalX=0 NormalY=0 NormalZ=1 AngleXU=0 Radius=0.855
    g5: Circle CenterX=44.8 CenterY=125 CenterZ=0 NormalX=0 NormalY=0 NormalZ=1 AngleXU=0 Radius=0.855
    g6: Circle CenterX=44.8 CenterY=104 CenterZ=0 NormalX=0 NormalY=0 NormalZ=1 AngleXU=0 Radius=0.855
    g7: Circle CenterX=-44.8 CenterY=30 CenterZ=0 NormalX=0 NormalY=0 NormalZ=1 AngleXU=0 Radius=0.855
    g8: Circle CenterX=44.8 CenterY=30 CenterZ=0 NormalX=0 NormalY=0 NormalZ=1 AngleXU=0 Radius=0.855
    g9: Circle CenterX=-44.8 CenterY=170 CenterZ=0 NormalX=0 NormalY=0 NormalZ=1 AngleXU=0 Radius=0.855
    g10: Circle CenterX=-44.8 CenterY=230 CenterZ=0 NormalX=0 NormalY=0 NormalZ=1 AngleXU=0 Radius=0.855
    g11: Circle CenterX=44.8 CenterY=230 CenterZ=0 NormalX=0 NormalY=0 NormalZ=1 AngleXU=0 Radius=0.855
  constraints (36):
    c: Diameter(g0) = 1.71
    c: Diameter(g1) = 1.71
    c: Diameter(g2) = 1.71
    c: Diameter(g3) = 1.71
    c: Diameter(g4) = 1.71
    c: Diameter(g5) = 1.71
    c: Diameter(g6) = 1.71
    c: Diameter(g7) = 1.71
    c: Diameter(g8) = 1.71
    c: Diameter(g9) = 1.71
    c: Vertical(g9,g1)
    c: Vertical(g1,g3)
    c: Vertical(g4,g3)
    c: Vertical(g7,g4)
    c: Vertical(g8,g6)
    c: Vertical(g6,g5)
    c: Vertical(g5,g2)
    c: Vertical(g0,g2)
    c: Horizontal(g2,g1)
    c: Horizontal(g3,g5)
    c: Horizontal(g4,g6)
    c: Horizontal(g7,g8)
    c: DistanceX(g7,g-1) = 44.8
    c: DistanceX(g-1,g8) = 44.8
    c: DistanceY(g-1,g7) = 30
    c: DistanceY(g-1,g4) = 104
    c: DistanceY(g-1,g3) = 125
    c: DistanceY(g-1,g1) = 145
    c: DistanceY(g-1,g9) = 170
    c: Diameter(g11) = 1.71
    c: Diameter(g10) = 1.71
    c: Horizontal(g9,g0)
    c: Vertical(g0,g11)
    c: Horizontal(g10,g11)
    c: Vertical(g10,g9)
    c: DistanceY(g-1,g10) = 230
FEATURE [PartDesign::Hole] Hole002  label="Plate Connection Holes"
  BaseFeature = -> Mirrored
  CustomThreadClearance = 0
  Depth = 25
  DepthType = 0
  Diameter = 1.71
  DrillForDepth = false
  DrillPoint = 1
  DrillPointAngle = 118
  HoleCutCountersinkAngle = 90
  HoleCutCustomValues = false
  HoleCutDepth = 0
  HoleCutDiameter = 3.5
  HoleCutType = 2
  ModelThread = false
  Placement = pos=(0,0,0) rot=(1,0,0;1.5708rad)
  Profile = -> Sketch017
  Suppressed = false
  Tapered = false
  TaperedAngle = 90
  ThreadClass = 0
  ThreadDepth = 25
  ThreadDepthType = 0
  ThreadDirection = 0
  ThreadFit = 0
  ThreadSize = 0
  ThreadType = 0
  Threaded = false
  UseCustomThreadClearance = false
  expr: Diameter = <<Monitor Chassis Parameters>>.GSTowerLayerJoinScrewDiameter
  expr: HoleCutDiameter = <<Monitor Chassis Parameters>>.GSM2BoltCountersinkDiameter
FEATURE [Part::Part2DObjectPython] ShapeString  label="Direction and ID ShapeString"  # Draft 2D object (typed FeaturePython)
  FontFile = <path>
  Fuse = false
  Justification = 6
  JustificationReference = 0
  KeepLeftMargin = false
  MakeFace = true
  ObliqueAngle = 0
  Placement = pos=(46.66,-0.3,5.22) rot=(0.57735,-0.57735,0.57735;2.0944rad)
  ScaleToSize = true
  Size = 5
  String = PiTrac                --> UP                                               --> UP
  Tracking = 0
FEATURE [PartDesign::Pocket] Pocket004  label="Direction and ID Pocket"
  BaseFeature = -> Hole002
  Direction = (1e-16,1,-2e-16)
  Length = 1
  Length2 = 5
  Placement = pos=(0,0,0) rot=(1,0,0;1.5708rad)
  Profile = -> ShapeString
  ReferenceAxis = -> ShapeString [N_Axis]
  Suppressed = false
  Type = 0
FEATURE [PartDesign::Body] Body  label="Backplate Body"
  AllowCompound = false
  Group = -> [Sketch,Sketch001,Pad,Pad001,Sketch002,Pad002,Sketch003,Hole,DatumPlane,Sketch004,Pad003,Mirrored,DatumPlane007,Sketch017,Hole002,ShapeString,Pocket004]
  Origin = -> Origin001
  Placement = pos=(0.2,-1,0) rot=(0,0,1;0rad)
  Tip = -> Pocket004
COMPONENT P1 — geometry summary ("PiTrac Pi Connector 1"; no construction recipe available for this part):
  bounding box: 100.0 x 60.0 x 13.0 mm
  tessellated surface: 62,712 triangles
  volume: 11365 mm^3 (15% of its bounding box)
PROVENANCE & LICENSES
A FreeCAD (.FCStd) document from a public repository crawl; recipes are the document's own serialized feature recipes (and, for linked parts, companion documents' recipes).
License: gpl-2.0.
